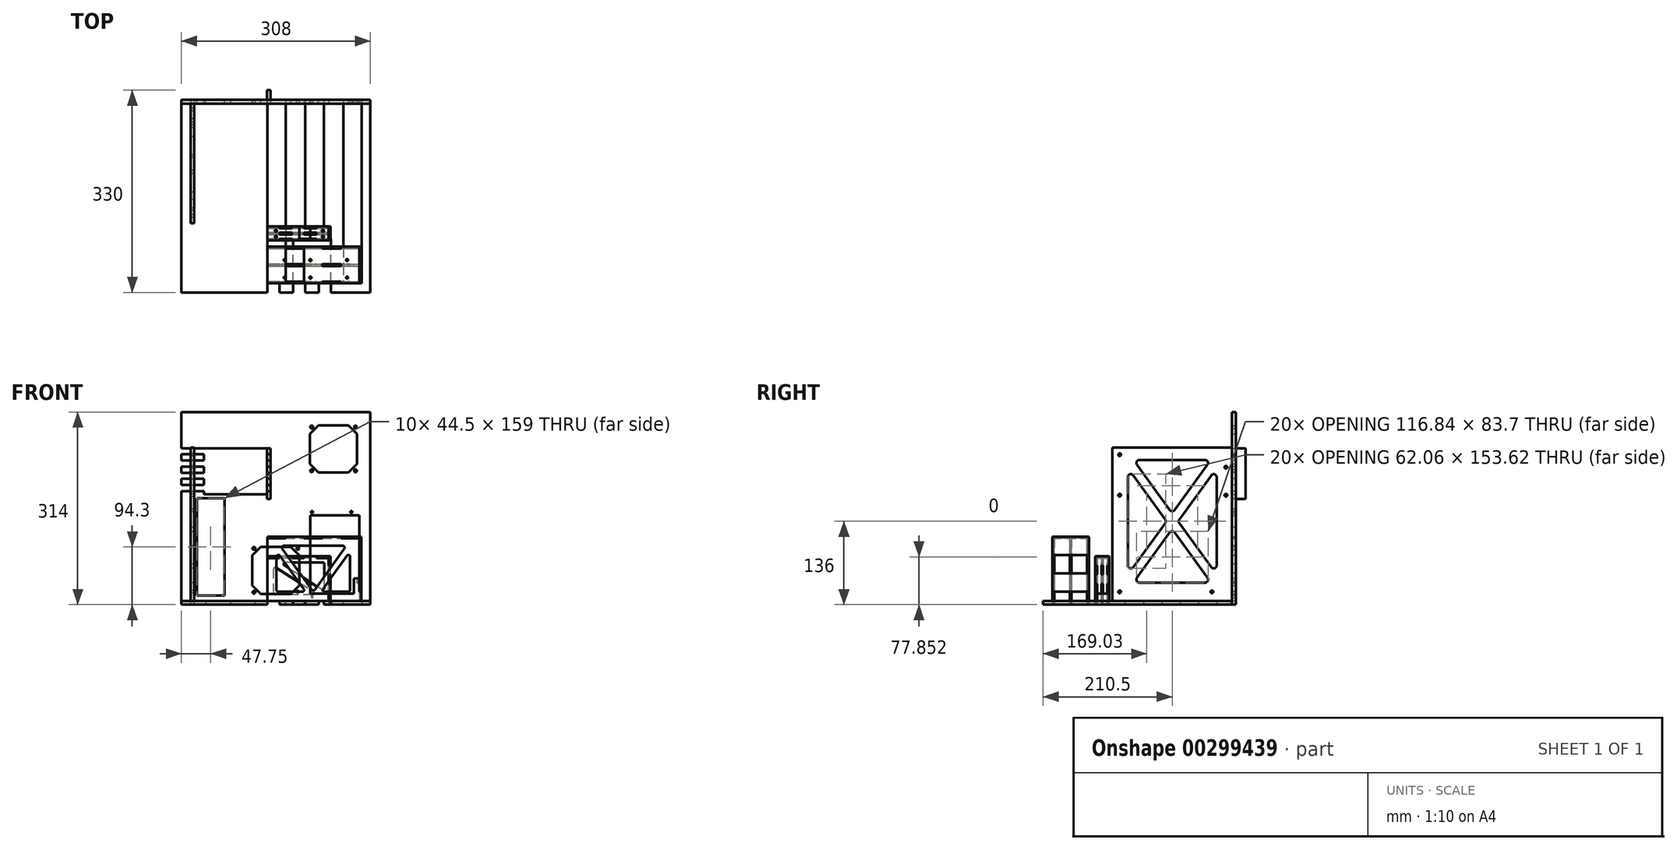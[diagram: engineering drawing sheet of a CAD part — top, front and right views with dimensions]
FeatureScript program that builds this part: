
annotation { "Feature Type Name" : "Feature", "Feature Type Description" : "" }
export const myFeature = defineFeature(function(context is Context, id is Id, definition is map)
    precondition{}
    {
        {
            var Q0;
            Q0=qCreatedBy(makeId("Top.planeOp"),FACE);
            var sketch = newSketch(context, id + "F0", { "sketchPlane" : qUnion([Q0])});
            skLineSegment(sketch, "E0.bottom", {"start": v(0, 0) * mm, "end": v(308, 0) * mm});
            skLineSegment(sketch, "E0.top", {"start": v(0, 314) * mm, "end": v(40, 314) * mm});
            skLineSegment(sketch, "E0.left", {"start": v(0, 0) * mm, "end": v(0, 314) * mm});
            skLineSegment(sketch, "E0.right", {"start": v(308, 0) * mm, "end": v(308, 308) * mm});
            skLineSegment(sketch, "E1.top", {"start": v(40, 308) * mm, "end": v(80, 308) * mm});
            skLineSegment(sketch, "E1.left", {"start": v(40, 314) * mm, "end": v(40, 308) * mm});
            skLineSegment(sketch, "E1.right", {"start": v(80, 314) * mm, "end": v(80, 308) * mm});
            skLineSegment(sketch, "E2.1.0.0", {"start": v(120, 314) * mm, "end": v(120, 308) * mm});
            skLineSegment(sketch, "E2.1.0.1", {"start": v(120, 308) * mm, "end": v(160, 308) * mm});
            skLineSegment(sketch, "E2.1.0.2", {"start": v(160, 314) * mm, "end": v(160, 308) * mm});
            skLineSegment(sketch, "E2.2.0.0", {"start": v(200, 314) * mm, "end": v(200, 308) * mm});
            skLineSegment(sketch, "E2.2.0.1", {"start": v(200, 308) * mm, "end": v(240, 308) * mm});
            skLineSegment(sketch, "E2.2.0.2", {"start": v(240, 314) * mm, "end": v(240, 308) * mm});
            skLineSegment(sketch, "E2.3.0.0", {"start": v(280, 314) * mm, "end": v(280, 308) * mm});
            skLineSegment(sketch, "E2.3.0.1", {"start": v(280, 308) * mm, "end": v(308, 308) * mm});
            skLineSegment(sketch, "E2.direction1", {"start": v(40, 308) * mm, "end": v(120, 308) * mm, "construction": true});
            skLineSegment(sketch, "E3.trimOffspring", {"start": v(160, 314) * mm, "end": v(200, 314) * mm});
            skLineSegment(sketch, "E4.trimOffspring", {"start": v(80, 314) * mm, "end": v(120, 314) * mm});
            skLineSegment(sketch, "E5.trimOffspring", {"start": v(240, 314) * mm, "end": v(280, 314) * mm});
            skSolve(sketch);
        }
        {
            var Q0;
            Q0 = qSketchRegion(id + "F0", true);
            extrude(context, id + "F1", {"entities" : qUnion([Q0]), "depth" : 6 * mm});
        }
        {
            var Q0;
            Q0=makeQuery(id+"F1.opExtrude","SWEPT_FACE",FACE,{"disambiguationData":[OSD([sQuery(id+"F0.wireOp",EDGE,"E0.top")])]});
            var sketch = newSketch(context, id + "F2", { "sketchPlane" : qUnion([Q0])});
            skLineSegment(sketch, "E6.bottom", {"start": v(0, 0) * mm, "end": v(-308, 0) * mm});
            skLineSegment(sketch, "E6.top", {"start": v(0, 314) * mm, "end": v(-308, 314) * mm});
            skLineSegment(sketch, "E6.left", {"start": v(0, 0) * mm, "end": v(0, 314) * mm});
            skLineSegment(sketch, "E6.right", {"start": v(-308, 0) * mm, "end": v(-308, 314) * mm});
            skSolve(sketch);
        }
        {
            var Q0;
            {var subQ4=sQuery(id+"F2.wireOp",EDGE,"E6.top");Q0=makeQuery(id+"F2.imprint","IMPRINT",FACE,{"disambiguationData":[TD([[makeQuery(id+"F2.imprint","IMPRINT",EDGE,{"derivedFrom":subQ4}),1.0]])]});}
            extrude(context, id + "F3", {"entities" : qUnion([Q0]), "oppositeDirection" : true, "depth" : 6 * mm});
        }
        {
            var Q0;
            Q0=makeQuery(id+"F1.opExtrude","SWEPT_BODY",BODY,{"disambiguationData":[OSD([sQuery(id+"F0.wireOp",EDGE,"E0.bottom"),sQuery(id+"F0.wireOp",EDGE,"E0.top"),sQuery(id+"F0.wireOp",EDGE,"E0.left"),sQuery(id+"F0.wireOp",EDGE,"E0.right"),sQuery(id+"F0.wireOp",EDGE,"E1.top"),sQuery(id+"F0.wireOp",EDGE,"E1.left"),sQuery(id+"F0.wireOp",EDGE,"E1.right"),sQuery(id+"F0.wireOp",EDGE,"E2.1.0.0"),sQuery(id+"F0.wireOp",EDGE,"E2.1.0.1"),sQuery(id+"F0.wireOp",EDGE,"E2.1.0.2"),sQuery(id+"F0.wireOp",EDGE,"E2.2.0.0"),sQuery(id+"F0.wireOp",EDGE,"E2.2.0.1"),sQuery(id+"F0.wireOp",EDGE,"E2.2.0.2"),sQuery(id+"F0.wireOp",EDGE,"E2.3.0.0"),sQuery(id+"F0.wireOp",EDGE,"E2.3.0.1"),sQuery(id+"F0.wireOp",EDGE,"E3.trimOffspring"),sQuery(id+"F0.wireOp",EDGE,"E4.trimOffspring"),sQuery(id+"F0.wireOp",EDGE,"E5.trimOffspring")])]});
            var Q1;
            Q1=makeQuery(id+"F3.opExtrude","SWEPT_BODY",BODY,{"disambiguationData":[OSD([sQuery(id+"F0.wireOp",EDGE,"E0.top"),sQuery(id+"F0.wireOp",EDGE,"E1.left"),sQuery(id+"F2.wireOp",EDGE,"E6.bottom"),sQuery(id+"F2.wireOp",EDGE,"E6.top"),sQuery(id+"F2.wireOp",EDGE,"E6.left"),sQuery(id+"F2.wireOp",EDGE,"E6.right")])]});
            booleanBodies(context, id + "F4", {"operationType" : BooleanOperationType.SUBTRACTION, "tools" : qUnion([Q0]), "targets" : qUnion([Q1]), "keepTools" : true});
        }
        {
            var Q0;
            Q0=makeQuery(id+"F1.opExtrude","SWEPT_FACE",FACE,{"disambiguationData":[OSD([sQuery(id+"F0.wireOp",EDGE,"E0.left")])]});
            cPlane(context, id + "F5", {"entities" : qUnion([Q0]), "cplaneType" : CPlaneType.OFFSET, "offset" : 15 * mm, "oppositeDirection" : true, "width" : 150 * mm, "height" : 150 * mm});
        }
        {
            var Q0;
            Q0=qCreatedBy(id+"F5.planeOp",FACE);
            var sketch = newSketch(context, id + "F6", { "sketchPlane" : qUnion([Q0])});
            skLineSegment(sketch, "E7.bottom", {"start": v(-284, 0) * mm, "end": v(-254, 0) * mm});
            skLineSegment(sketch, "E7.top", {"start": v(-308, 256) * mm, "end": v(-113, 256) * mm});
            skLineSegment(sketch, "E7.left", {"start": v(-314, 36) * mm, "end": v(-314, 66) * mm});
            skLineSegment(sketch, "E7.right", {"start": v(-113, 6) * mm, "end": v(-113, 256) * mm});
            skPoint(sketch, "E8", {"position": v(-298, 224.2) * mm});
            skPoint(sketch, "E9", {"position": v(-124.85, 244.52) * mm});
            skPoint(sketch, "E10", {"position": v(-124.85, 178.48) * mm});
            skPoint(sketch, "E11", {"position": v(-298, 178.48) * mm});
            skPoint(sketch, "E12", {"position": v(-275.14, 21) * mm});
            skPoint(sketch, "E13", {"position": v(-124.85, 21) * mm});
            skLineSegment(sketch, "E14.top", {"start": v(-308, 6) * mm, "end": v(-284, 6) * mm});
            skLineSegment(sketch, "E14.right", {"start": v(-284, 0) * mm, "end": v(-284, 6) * mm});
            skLineSegment(sketch, "E15.1.0.0", {"start": v(-224, 0) * mm, "end": v(-224, 6) * mm});
            skLineSegment(sketch, "E15.1.0.1", {"start": v(-254, 6) * mm, "end": v(-224, 6) * mm});
            skLineSegment(sketch, "E15.1.0.2", {"start": v(-254, 0) * mm, "end": v(-254, 6) * mm});
            skLineSegment(sketch, "E15.2.0.0", {"start": v(-164, 0) * mm, "end": v(-164, 6) * mm});
            skLineSegment(sketch, "E15.2.0.1", {"start": v(-194, 6) * mm, "end": v(-164, 6) * mm});
            skLineSegment(sketch, "E15.2.0.2", {"start": v(-194, 0) * mm, "end": v(-194, 6) * mm});
            skLineSegment(sketch, "E15.3.0.1", {"start": v(-134, 6) * mm, "end": v(-113, 6) * mm});
            skLineSegment(sketch, "E15.3.0.2", {"start": v(-134, 0) * mm, "end": v(-134, 6) * mm});
            skLineSegment(sketch, "E15.direction1", {"start": v(-284, 0) * mm, "end": v(-254, 0) * mm, "construction": true});
            skLineSegment(sketch, "E16.trimOffspring", {"start": v(-164, 0) * mm, "end": v(-134, 0) * mm});
            skLineSegment(sketch, "E17.trimOffspring", {"start": v(-224, 0) * mm, "end": v(-194, 0) * mm});
            skLineSegment(sketch, "E18.top", {"start": v(-314, 36) * mm, "end": v(-308, 36) * mm});
            skLineSegment(sketch, "E18.right", {"start": v(-308, 6) * mm, "end": v(-308, 36) * mm});
            skLineSegment(sketch, "E19.0.1.0", {"start": v(-308, 66) * mm, "end": v(-308, 96) * mm});
            skLineSegment(sketch, "E19.0.1.1", {"start": v(-314, 96) * mm, "end": v(-308, 96) * mm});
            skLineSegment(sketch, "E19.0.1.2", {"start": v(-314, 66) * mm, "end": v(-308, 66) * mm});
            skLineSegment(sketch, "E19.0.2.0", {"start": v(-308, 126) * mm, "end": v(-308, 156) * mm});
            skLineSegment(sketch, "E19.0.2.1", {"start": v(-314, 156) * mm, "end": v(-308, 156) * mm});
            skLineSegment(sketch, "E19.0.2.2", {"start": v(-314, 126) * mm, "end": v(-308, 126) * mm});
            skLineSegment(sketch, "E19.0.3.0", {"start": v(-308, 186) * mm, "end": v(-308, 216) * mm});
            skLineSegment(sketch, "E19.0.3.1", {"start": v(-314, 216) * mm, "end": v(-308, 216) * mm});
            skLineSegment(sketch, "E19.0.3.2", {"start": v(-314, 186) * mm, "end": v(-308, 186) * mm});
            skLineSegment(sketch, "E19.0.4.0", {"start": v(-308, 246) * mm, "end": v(-308, 256) * mm});
            skLineSegment(sketch, "E19.0.4.2", {"start": v(-314, 246) * mm, "end": v(-308, 246) * mm});
            skLineSegment(sketch, "E19.direction1", {"start": v(-325.44, 6) * mm, "end": v(-314, 6) * mm, "construction": true});
            skLineSegment(sketch, "E19.direction2", {"start": v(-314, 36) * mm, "end": v(-314, 66) * mm, "construction": true});
            skLineSegment(sketch, "E20.trimOffspring", {"start": v(-314, 96) * mm, "end": v(-314, 126) * mm});
            skLineSegment(sketch, "E21.trimOffspring", {"start": v(-314, 156) * mm, "end": v(-314, 186) * mm});
            skLineSegment(sketch, "E22.trimOffspring", {"start": v(-314, 216) * mm, "end": v(-314, 246) * mm});
            skLineSegment(sketch, "E23.bottom", {"start": v(-283, 236) * mm, "end": v(-138, 236) * mm, "construction": true});
            skLineSegment(sketch, "E23.top", {"start": v(-283, 36) * mm, "end": v(-138, 36) * mm, "construction": true});
            skLineSegment(sketch, "E23.left", {"start": v(-283, 236) * mm, "end": v(-283, 36) * mm, "construction": true});
            skLineSegment(sketch, "E23.right", {"start": v(-138, 236) * mm, "end": v(-138, 36) * mm, "construction": true});
            skLineSegment(sketch, "E24", {"start": v(-283, 236) * mm, "end": v(-138, 36) * mm, "construction": true});
            skLineSegment(sketch, "E25", {"start": v(-283, 36) * mm, "end": v(-138, 236) * mm, "construction": true});
            skLineSegment(sketch, "E26", {"start": v(-138, 223.22) * mm, "end": v(-201.24, 136) * mm});
            skLineSegment(sketch, "E27", {"start": v(-201.24, 136) * mm, "end": v(-138, 48.78) * mm});
            skLineSegment(sketch, "E28", {"start": v(-147.26, 236) * mm, "end": v(-210.5, 148.78) * mm});
            skLineSegment(sketch, "E29", {"start": v(-210.5, 148.78) * mm, "end": v(-273.74, 236) * mm});
            skLineSegment(sketch, "E30", {"start": v(-147.26, 36) * mm, "end": v(-210.5, 123.22) * mm});
            skLineSegment(sketch, "E31", {"start": v(-210.5, 123.22) * mm, "end": v(-273.74, 36) * mm});
            skLineSegment(sketch, "E32", {"start": v(-283, 223.22) * mm, "end": v(-219.76, 136) * mm});
            skLineSegment(sketch, "E33", {"start": v(-219.76, 136) * mm, "end": v(-283, 48.78) * mm});
            skLineSegment(sketch, "E34", {"start": v(-273.74, 36) * mm, "end": v(-147.26, 36) * mm});
            skLineSegment(sketch, "E35", {"start": v(-138, 223.22) * mm, "end": v(-138, 48.78) * mm});
            skLineSegment(sketch, "E36", {"start": v(-273.74, 236) * mm, "end": v(-147.26, 236) * mm});
            skLineSegment(sketch, "E37", {"start": v(-283, 223.22) * mm, "end": v(-283, 48.78) * mm});
            skSolve(sketch);
        }
        {
            var Q0;
            Q0=makeQuery(id+"F6.imprint","IMPRINT",FACE,{"disambiguationData":[TD([[makeQuery(id+"F6.imprint","IMPRINT",EDGE,{"derivedFrom":sQuery(id+"F6.wireOp",EDGE,"E7.bottom")}),1.0]])]});
            extrude(context, id + "F7", {"entities" : qUnion([Q0]), "oppositeDirection" : true, "depth" : 6 * mm});
        }
        {
            var Q0;
            Q0=makeQuery(id+"F7.opExtrude","SWEPT_BODY",BODY,{"disambiguationData":[OSD([sQuery(id+"F6.wireOp",EDGE,"E7.bottom"),sQuery(id+"F6.wireOp",EDGE,"E7.top"),sQuery(id+"F6.wireOp",EDGE,"E7.left"),sQuery(id+"F6.wireOp",EDGE,"E7.right"),sQuery(id+"F6.wireOp",EDGE,"E14.top"),sQuery(id+"F6.wireOp",EDGE,"E14.right"),sQuery(id+"F6.wireOp",EDGE,"E15.1.0.0"),sQuery(id+"F6.wireOp",EDGE,"E15.1.0.1"),sQuery(id+"F6.wireOp",EDGE,"E15.1.0.2"),sQuery(id+"F6.wireOp",EDGE,"E15.2.0.0"),sQuery(id+"F6.wireOp",EDGE,"E15.2.0.1"),sQuery(id+"F6.wireOp",EDGE,"E15.2.0.2"),sQuery(id+"F6.wireOp",EDGE,"E15.3.0.1"),sQuery(id+"F6.wireOp",EDGE,"E15.3.0.2"),sQuery(id+"F6.wireOp",EDGE,"E16.trimOffspring"),sQuery(id+"F6.wireOp",EDGE,"E17.trimOffspring"),sQuery(id+"F6.wireOp",EDGE,"E18.top"),sQuery(id+"F6.wireOp",EDGE,"E18.right"),sQuery(id+"F6.wireOp",EDGE,"E19.0.1.0"),sQuery(id+"F6.wireOp",EDGE,"E19.0.1.1"),sQuery(id+"F6.wireOp",EDGE,"E19.0.1.2"),sQuery(id+"F6.wireOp",EDGE,"E19.0.2.0"),sQuery(id+"F6.wireOp",EDGE,"E19.0.2.1"),sQuery(id+"F6.wireOp",EDGE,"E19.0.2.2"),sQuery(id+"F6.wireOp",EDGE,"E19.0.3.0"),sQuery(id+"F6.wireOp",EDGE,"E19.0.3.1"),sQuery(id+"F6.wireOp",EDGE,"E19.0.3.2"),sQuery(id+"F6.wireOp",EDGE,"E19.0.4.0"),sQuery(id+"F6.wireOp",EDGE,"E19.0.4.2"),sQuery(id+"F6.wireOp",EDGE,"E20.trimOffspring"),sQuery(id+"F6.wireOp",EDGE,"E21.trimOffspring"),sQuery(id+"F6.wireOp",EDGE,"E22.trimOffspring")])]});
            var Q1;
            Q1=makeQuery(id+"F3.opExtrude","SWEPT_BODY",BODY,{"disambiguationData":[OSD([sQuery(id+"F0.wireOp",EDGE,"E0.top"),sQuery(id+"F0.wireOp",EDGE,"E1.left"),sQuery(id+"F2.wireOp",EDGE,"E6.bottom"),sQuery(id+"F2.wireOp",EDGE,"E6.top"),sQuery(id+"F2.wireOp",EDGE,"E6.left"),sQuery(id+"F2.wireOp",EDGE,"E6.right")])]});
            booleanBodies(context, id + "F8", {"operationType" : BooleanOperationType.SUBTRACTION, "tools" : qUnion([Q0]), "targets" : qUnion([Q1]), "keepTools" : true});
        }
        {
            var Q0;
            Q0=makeQuery(id+"F7.opExtrude","SWEPT_BODY",BODY,{"disambiguationData":[OSD([sQuery(id+"F6.wireOp",EDGE,"E7.bottom"),sQuery(id+"F6.wireOp",EDGE,"E7.top"),sQuery(id+"F6.wireOp",EDGE,"E7.left"),sQuery(id+"F6.wireOp",EDGE,"E7.right"),sQuery(id+"F6.wireOp",EDGE,"E14.top"),sQuery(id+"F6.wireOp",EDGE,"E14.right"),sQuery(id+"F6.wireOp",EDGE,"E15.1.0.0"),sQuery(id+"F6.wireOp",EDGE,"E15.1.0.1"),sQuery(id+"F6.wireOp",EDGE,"E15.1.0.2"),sQuery(id+"F6.wireOp",EDGE,"E15.2.0.0"),sQuery(id+"F6.wireOp",EDGE,"E15.2.0.1"),sQuery(id+"F6.wireOp",EDGE,"E15.2.0.2"),sQuery(id+"F6.wireOp",EDGE,"E15.3.0.1"),sQuery(id+"F6.wireOp",EDGE,"E15.3.0.2"),sQuery(id+"F6.wireOp",EDGE,"E16.trimOffspring"),sQuery(id+"F6.wireOp",EDGE,"E17.trimOffspring"),sQuery(id+"F6.wireOp",EDGE,"E18.top"),sQuery(id+"F6.wireOp",EDGE,"E18.right"),sQuery(id+"F6.wireOp",EDGE,"E19.0.1.0"),sQuery(id+"F6.wireOp",EDGE,"E19.0.1.1"),sQuery(id+"F6.wireOp",EDGE,"E19.0.1.2"),sQuery(id+"F6.wireOp",EDGE,"E19.0.2.0"),sQuery(id+"F6.wireOp",EDGE,"E19.0.2.1"),sQuery(id+"F6.wireOp",EDGE,"E19.0.2.2"),sQuery(id+"F6.wireOp",EDGE,"E19.0.3.0"),sQuery(id+"F6.wireOp",EDGE,"E19.0.3.1"),sQuery(id+"F6.wireOp",EDGE,"E19.0.3.2"),sQuery(id+"F6.wireOp",EDGE,"E19.0.4.0"),sQuery(id+"F6.wireOp",EDGE,"E19.0.4.2"),sQuery(id+"F6.wireOp",EDGE,"E20.trimOffspring"),sQuery(id+"F6.wireOp",EDGE,"E21.trimOffspring"),sQuery(id+"F6.wireOp",EDGE,"E22.trimOffspring")])]});
            var Q1;
            Q1=makeQuery(id+"F1.opExtrude","SWEPT_BODY",BODY,{"disambiguationData":[OSD([sQuery(id+"F0.wireOp",EDGE,"E0.bottom"),sQuery(id+"F0.wireOp",EDGE,"E0.top"),sQuery(id+"F0.wireOp",EDGE,"E0.left"),sQuery(id+"F0.wireOp",EDGE,"E0.right"),sQuery(id+"F0.wireOp",EDGE,"E1.top"),sQuery(id+"F0.wireOp",EDGE,"E1.left"),sQuery(id+"F0.wireOp",EDGE,"E1.right"),sQuery(id+"F0.wireOp",EDGE,"E2.1.0.0"),sQuery(id+"F0.wireOp",EDGE,"E2.1.0.1"),sQuery(id+"F0.wireOp",EDGE,"E2.1.0.2"),sQuery(id+"F0.wireOp",EDGE,"E2.2.0.0"),sQuery(id+"F0.wireOp",EDGE,"E2.2.0.1"),sQuery(id+"F0.wireOp",EDGE,"E2.2.0.2"),sQuery(id+"F0.wireOp",EDGE,"E2.3.0.0"),sQuery(id+"F0.wireOp",EDGE,"E2.3.0.1"),sQuery(id+"F0.wireOp",EDGE,"E3.trimOffspring"),sQuery(id+"F0.wireOp",EDGE,"E4.trimOffspring"),sQuery(id+"F0.wireOp",EDGE,"E5.trimOffspring")])]});
            booleanBodies(context, id + "F9", {"operationType" : BooleanOperationType.SUBTRACTION, "tools" : qUnion([Q0]), "targets" : qUnion([Q1]), "keepTools" : true});
        }
        {
            var Q0;
            Q0=sQuery(id+"F6.wireOp",VERTEX,"E8");
            var Q1;
            Q1=sQuery(id+"F6.wireOp",VERTEX,"E11");
            var Q2;
            Q2=sQuery(id+"F6.wireOp",VERTEX,"E12");
            var Q3;
            Q3=sQuery(id+"F6.wireOp",VERTEX,"E13");
            var Q4;
            Q4=sQuery(id+"F6.wireOp",VERTEX,"E10");
            var Q5;
            Q5=sQuery(id+"F6.wireOp",VERTEX,"E9");
            var Q6;
            Q6=makeQuery(id+"F7.opExtrude","SWEPT_BODY",BODY,{"disambiguationData":[OSD([sQuery(id+"F6.wireOp",EDGE,"E7.bottom"),sQuery(id+"F6.wireOp",EDGE,"E7.top"),sQuery(id+"F6.wireOp",EDGE,"E7.left"),sQuery(id+"F6.wireOp",EDGE,"E7.right"),sQuery(id+"F6.wireOp",EDGE,"E14.top"),sQuery(id+"F6.wireOp",EDGE,"E14.right"),sQuery(id+"F6.wireOp",EDGE,"E15.1.0.0"),sQuery(id+"F6.wireOp",EDGE,"E15.1.0.1"),sQuery(id+"F6.wireOp",EDGE,"E15.1.0.2"),sQuery(id+"F6.wireOp",EDGE,"E15.2.0.0"),sQuery(id+"F6.wireOp",EDGE,"E15.2.0.1"),sQuery(id+"F6.wireOp",EDGE,"E15.2.0.2"),sQuery(id+"F6.wireOp",EDGE,"E15.3.0.1"),sQuery(id+"F6.wireOp",EDGE,"E15.3.0.2"),sQuery(id+"F6.wireOp",EDGE,"E16.trimOffspring"),sQuery(id+"F6.wireOp",EDGE,"E17.trimOffspring"),sQuery(id+"F6.wireOp",EDGE,"E18.top"),sQuery(id+"F6.wireOp",EDGE,"E18.right"),sQuery(id+"F6.wireOp",EDGE,"E19.0.1.0"),sQuery(id+"F6.wireOp",EDGE,"E19.0.1.1"),sQuery(id+"F6.wireOp",EDGE,"E19.0.1.2"),sQuery(id+"F6.wireOp",EDGE,"E19.0.2.0"),sQuery(id+"F6.wireOp",EDGE,"E19.0.2.1"),sQuery(id+"F6.wireOp",EDGE,"E19.0.2.2"),sQuery(id+"F6.wireOp",EDGE,"E19.0.3.0"),sQuery(id+"F6.wireOp",EDGE,"E19.0.3.1"),sQuery(id+"F6.wireOp",EDGE,"E19.0.3.2"),sQuery(id+"F6.wireOp",EDGE,"E19.0.4.0"),sQuery(id+"F6.wireOp",EDGE,"E19.0.4.2"),sQuery(id+"F6.wireOp",EDGE,"E20.trimOffspring"),sQuery(id+"F6.wireOp",EDGE,"E21.trimOffspring"),sQuery(id+"F6.wireOp",EDGE,"E22.trimOffspring")])]});
            hole(context, id + "F10", {"style" : HoleStyle.SIMPLE, "endStyle" : HoleEndStyle.THROUGH, "standardTappedOrClearance" : lookupTablePath({ "standard" : "ISO", "fit" : "Normal", "size" : "M4", "type" : "Clearance" }), "standardBlindInLast" : lookupTablePath({ "fit" : "Standard", "standard" : "ISO", "size" : "M4", "type" : "Clearance" }), "holeDiameter" : 4.4 * mm, "tappedDepth" : 6 * mm, "tapClearance" : 3, "locations" : qUnion([Q0, Q1, Q2, Q3, Q4, Q5]), "scope" : qUnion([Q6])});
        }
        {
            var Q0;
            Q0=makeQuery(id+"F7.opExtrude","SWEPT_EDGE",EDGE,{"disambiguationData":[OSD([sQuery(id+"F6.wireOp",EDGE,"E32"),sQuery(id+"F6.wireOp",EDGE,"E37")])]});
            var Q1;
            Q1=makeQuery(id+"F7.opExtrude","SWEPT_EDGE",EDGE,{"disambiguationData":[OSD([sQuery(id+"F6.wireOp",EDGE,"E30"),sQuery(id+"F6.wireOp",EDGE,"E31")])]});
            var Q2;
            Q2=makeQuery(id+"F7.opExtrude","SWEPT_EDGE",EDGE,{"disambiguationData":[OSD([sQuery(id+"F6.wireOp",EDGE,"E30"),sQuery(id+"F6.wireOp",EDGE,"E34")])]});
            var Q3;
            Q3=makeQuery(id+"F7.opExtrude","SWEPT_EDGE",EDGE,{"disambiguationData":[OSD([sQuery(id+"F6.wireOp",EDGE,"E27"),sQuery(id+"F6.wireOp",EDGE,"E35")])]});
            var Q4;
            Q4=makeQuery(id+"F7.opExtrude","SWEPT_EDGE",EDGE,{"disambiguationData":[OSD([sQuery(id+"F6.wireOp",EDGE,"E26"),sQuery(id+"F6.wireOp",EDGE,"E27")])]});
            var Q5;
            Q5=makeQuery(id+"F7.opExtrude","SWEPT_EDGE",EDGE,{"disambiguationData":[OSD([sQuery(id+"F6.wireOp",EDGE,"E26"),sQuery(id+"F6.wireOp",EDGE,"E35")])]});
            var Q6;
            Q6=makeQuery(id+"F7.opExtrude","SWEPT_EDGE",EDGE,{"disambiguationData":[OSD([sQuery(id+"F6.wireOp",EDGE,"E28"),sQuery(id+"F6.wireOp",EDGE,"E36")])]});
            var Q7;
            Q7=makeQuery(id+"F7.opExtrude","SWEPT_EDGE",EDGE,{"disambiguationData":[OSD([sQuery(id+"F6.wireOp",EDGE,"E28"),sQuery(id+"F6.wireOp",EDGE,"E29")])]});
            var Q8;
            Q8=makeQuery(id+"F7.opExtrude","SWEPT_EDGE",EDGE,{"disambiguationData":[OSD([sQuery(id+"F6.wireOp",EDGE,"E32"),sQuery(id+"F6.wireOp",EDGE,"E33")])]});
            var Q9;
            Q9=makeQuery(id+"F7.opExtrude","SWEPT_EDGE",EDGE,{"disambiguationData":[OSD([sQuery(id+"F6.wireOp",EDGE,"E33"),sQuery(id+"F6.wireOp",EDGE,"E37")])]});
            var Q10;
            Q10=makeQuery(id+"F7.opExtrude","SWEPT_EDGE",EDGE,{"disambiguationData":[OSD([sQuery(id+"F6.wireOp",EDGE,"E31"),sQuery(id+"F6.wireOp",EDGE,"E34")])]});
            var Q11;
            Q11=makeQuery(id+"F7.opExtrude","SWEPT_EDGE",EDGE,{"disambiguationData":[OSD([sQuery(id+"F6.wireOp",EDGE,"E29"),sQuery(id+"F6.wireOp",EDGE,"E36")])]});
            fillet(context, id + "F11", {"entities" : qUnion([Q0, Q1, Q2, Q3, Q4, Q5, Q6, Q7, Q8, Q9, Q10, Q11]), "radius" : 5 * mm, "tangentPropagation" : true, "allowEdgeOverflow" : false});
        }
        {
            var Q0;
            Q0=makeQuery(id+"F3.opExtrude","CAP_FACE",FACE,{"disambiguationData":[OSD([sQuery(id+"F0.wireOp",EDGE,"E0.top"),sQuery(id+"F0.wireOp",EDGE,"E1.left"),sQuery(id+"F2.wireOp",EDGE,"E6.bottom"),sQuery(id+"F2.wireOp",EDGE,"E6.top"),sQuery(id+"F2.wireOp",EDGE,"E6.left"),sQuery(id+"F2.wireOp",EDGE,"E6.right")])],"isStart":true});
            var sketch = newSketch(context, id + "F12", { "sketchPlane" : qUnion([Q0])});
            skLineSegment(sketch, "E38", {"start": v(-27.8, 249.88) * mm, "end": v(-27.8, 20.43) * mm, "construction": true});
            skLineSegment(sketch, "E39.bottom", {"start": v(-70, 14.8) * mm, "end": v(-25.5, 14.8) * mm});
            skLineSegment(sketch, "E39.top", {"start": v(-70, 173.8) * mm, "end": v(-25.5, 173.8) * mm});
            skLineSegment(sketch, "E39.left", {"start": v(-70, 14.8) * mm, "end": v(-70, 173.8) * mm});
            skLineSegment(sketch, "E39.right", {"start": v(-25.5, 14.8) * mm, "end": v(-25.5, 173.8) * mm});
            skLineSegment(sketch, "E40.bottom", {"start": v(-139.3, 180.15) * mm, "end": v(-36.6, 180.15) * mm});
            skLineSegment(sketch, "E40.top", {"start": v(-139.3, 255.08) * mm, "end": v(-36.6, 255.08) * mm});
            skLineSegment(sketch, "E40.left", {"start": v(-139.3, 180.15) * mm, "end": v(-139.3, 255.08) * mm});
            skLineSegment(sketch, "E40.right", {"start": v(-36.6, 180.15) * mm, "end": v(-36.6, 255.08) * mm});
            skLineSegment(sketch, "E41", {"start": v(-139.3, 172.88) * mm, "end": v(-139.3, 270.63) * mm, "construction": true});
            skSolve(sketch);
        }
        {
            var Q0;
            Q0 = qSketchRegion(id + "F12", true);
            extrude(context, id + "F13", {"entities" : qUnion([Q0]), "operationType" : NewBodyOperationType.REMOVE, "endBound" : BoundingType.THROUGH_ALL, "oppositeDirection" : true, "depth" : 25 * mm});
        }
        {
            var Q0;
            Q0=sQuery(id+"F12.wireOp",EDGE,"E41");
            var Q1;
            Q1=qCreatedBy(makeId("Right.planeOp"),FACE);
            cPlane(context, id + "F14", {"entities" : qUnion([Q0, Q1]), "cplaneType" : CPlaneType.LINE_ANGLE, "offset" : 25 * mm, "angle" : 0 * degree, "width" : 150 * mm, "height" : 150 * mm});
        }
        {
            var Q0;
            Q0=qCreatedBy(id+"F14.planeOp",FACE);
            var sketch = newSketch(context, id + "F15", { "sketchPlane" : qUnion([Q0])});
            skLineSegment(sketch, "E42", {"start": v(-345.36, 180.15) * mm, "end": v(-318, 180.15) * mm, "construction": true});
            skLineSegment(sketch, "E43.bottom", {"start": v(-330, 255.08) * mm, "end": v(-308, 255.08) * mm});
            skLineSegment(sketch, "E43.top", {"start": v(-330, 172.15) * mm, "end": v(-308, 172.15) * mm});
            skLineSegment(sketch, "E43.left", {"start": v(-330, 255.08) * mm, "end": v(-330, 172.15) * mm});
            skLineSegment(sketch, "E43.right", {"start": v(-308, 255.08) * mm, "end": v(-308, 172.15) * mm});
            skSolve(sketch);
        }
        {
            var Q0;
            Q0 = qSketchRegion(id + "F15", true);
            extrude(context, id + "F16", {"entities" : qUnion([Q0]), "oppositeDirection" : true, "depth" : 6 * mm});
        }
        {
            var Q0;
            Q0=makeQuery(id+"F16.opExtrude","CAP_FACE",FACE,{"disambiguationData":[OSD([sQuery(id+"F15.wireOp",EDGE,"E43.bottom"),sQuery(id+"F15.wireOp",EDGE,"E43.top"),sQuery(id+"F15.wireOp",EDGE,"E43.left"),sQuery(id+"F15.wireOp",EDGE,"E43.right")])],"isStart":false});
            var sketch = newSketch(context, id + "F17", { "sketchPlane" : qUnion([Q0])});
            skLineSegment(sketch, "E44.bottom", {"start": v(308, 255.08) * mm, "end": v(314, 255.08) * mm});
            skLineSegment(sketch, "E44.top", {"start": v(308, 245.08) * mm, "end": v(314, 245.08) * mm});
            skLineSegment(sketch, "E44.left", {"start": v(308, 255.08) * mm, "end": v(308, 245.08) * mm});
            skLineSegment(sketch, "E44.right", {"start": v(314, 255.08) * mm, "end": v(314, 245.08) * mm});
            skLineSegment(sketch, "E45.0.1.0", {"start": v(308, 225.08) * mm, "end": v(314, 225.08) * mm});
            skLineSegment(sketch, "E45.0.1.1", {"start": v(314, 235.08) * mm, "end": v(314, 225.08) * mm});
            skLineSegment(sketch, "E45.0.1.2", {"start": v(308, 235.08) * mm, "end": v(314, 235.08) * mm});
            skLineSegment(sketch, "E45.0.1.3", {"start": v(308, 235.08) * mm, "end": v(308, 225.08) * mm});
            skLineSegment(sketch, "E45.0.2.0", {"start": v(308, 205.08) * mm, "end": v(314, 205.08) * mm});
            skLineSegment(sketch, "E45.0.2.1", {"start": v(314, 215.08) * mm, "end": v(314, 205.08) * mm});
            skLineSegment(sketch, "E45.0.2.2", {"start": v(308, 215.08) * mm, "end": v(314, 215.08) * mm});
            skLineSegment(sketch, "E45.0.2.3", {"start": v(308, 215.08) * mm, "end": v(308, 205.08) * mm});
            skLineSegment(sketch, "E45.0.3.0", {"start": v(308, 185.08) * mm, "end": v(314, 185.08) * mm});
            skLineSegment(sketch, "E45.0.3.1", {"start": v(314, 195.08) * mm, "end": v(314, 185.08) * mm});
            skLineSegment(sketch, "E45.0.3.2", {"start": v(308, 195.08) * mm, "end": v(314, 195.08) * mm});
            skLineSegment(sketch, "E45.0.3.3", {"start": v(308, 195.08) * mm, "end": v(308, 185.08) * mm});
            skLineSegment(sketch, "E45.direction1", {"start": v(308, 245.08) * mm, "end": v(333, 245.08) * mm, "construction": true});
            skLineSegment(sketch, "E45.direction2", {"start": v(308, 245.08) * mm, "end": v(308, 225.08) * mm, "construction": true});
            skSolve(sketch);
        }
        {
            var Q0;
            Q0 = qSketchRegion(id + "F17", true);
            extrude(context, id + "F18", {"entities" : qUnion([Q0]), "operationType" : NewBodyOperationType.REMOVE, "endBound" : BoundingType.THROUGH_ALL, "oppositeDirection" : true, "depth" : 25 * mm});
        }
        {
            var Q0;
            Q0=makeQuery(id+"F16.opExtrude","SWEPT_BODY",BODY,{"disambiguationData":[OSD([sQuery(id+"F15.wireOp",EDGE,"E43.bottom"),sQuery(id+"F15.wireOp",EDGE,"E43.top"),sQuery(id+"F15.wireOp",EDGE,"E43.left"),sQuery(id+"F15.wireOp",EDGE,"E43.right")])]});
            var Q1;
            Q1=makeQuery(id+"F3.opExtrude","SWEPT_BODY",BODY,{"disambiguationData":[OSD([sQuery(id+"F0.wireOp",EDGE,"E0.top"),sQuery(id+"F0.wireOp",EDGE,"E1.left"),sQuery(id+"F2.wireOp",EDGE,"E6.bottom"),sQuery(id+"F2.wireOp",EDGE,"E6.top"),sQuery(id+"F2.wireOp",EDGE,"E6.left"),sQuery(id+"F2.wireOp",EDGE,"E6.right")])]});
            booleanBodies(context, id + "F19", {"operationType" : BooleanOperationType.SUBTRACTION, "tools" : qUnion([Q0]), "targets" : qUnion([Q1]), "keepTools" : true});
        }
        {
            var Q0;
            Q0=makeQuery(id+"F3.opExtrude","CAP_FACE",FACE,{"disambiguationData":[OSD([sQuery(id+"F0.wireOp",EDGE,"E0.top"),sQuery(id+"F0.wireOp",EDGE,"E1.left"),sQuery(id+"F2.wireOp",EDGE,"E6.bottom"),sQuery(id+"F2.wireOp",EDGE,"E6.top"),sQuery(id+"F2.wireOp",EDGE,"E6.left"),sQuery(id+"F2.wireOp",EDGE,"E6.right")])],"isStart":true});
            var sketch = newSketch(context, id + "F20", { "sketchPlane" : qUnion([Q0])});
            skPoint(sketch, "E46", {"position": v(-213, 13) * mm});
            skPoint(sketch, "E47", {"position": v(-287, 37) * mm});
            skPoint(sketch, "E48", {"position": v(-277, 151) * mm});
            skPoint(sketch, "E49", {"position": v(-213, 151) * mm});
            skLineSegment(sketch, "E50", {"start": v(-293, 0) * mm, "end": v(-293, 156) * mm, "construction": true});
            skLineSegment(sketch, "E51", {"start": v(-207, 0) * mm, "end": v(-207, 156) * mm, "construction": true});
            skLineSegment(sketch, "E52", {"start": v(-293, 156) * mm, "end": v(-207, 156) * mm, "construction": true});
            skLineSegment(sketch, "E53.bottom", {"start": v(-290, 146) * mm, "end": v(-210, 146) * mm});
            skLineSegment(sketch, "E53.top", {"start": v(-281, 18) * mm, "end": v(-210, 18) * mm});
            skLineSegment(sketch, "E53.right", {"start": v(-210, 146) * mm, "end": v(-210, 18) * mm});
            skLineSegment(sketch, "E54", {"start": v(-290, 146) * mm, "end": v(-290, 43) * mm});
            skLineSegment(sketch, "E55", {"start": v(-290, 43) * mm, "end": v(-281, 43) * mm});
            skLineSegment(sketch, "E56", {"start": v(-281, 18) * mm, "end": v(-281, 43) * mm});
            skSolve(sketch);
        }
        {
            var Q0;
            Q0=makeQuery(id+"F20.imprint","IMPRINT",FACE,{"disambiguationData":[TD([[makeQuery(id+"F20.imprint","IMPRINT",EDGE,{"derivedFrom":sQuery(id+"F20.wireOp",EDGE,"E53.bottom")}),-1.0]])]});
            extrude(context, id + "F21", {"entities" : qUnion([Q0]), "operationType" : NewBodyOperationType.REMOVE, "endBound" : BoundingType.THROUGH_ALL, "oppositeDirection" : true, "depth" : 25 * mm});
        }
        {
            var Q0;
            Q0=sQuery(id+"F20.wireOp",VERTEX,"E48");
            var Q1;
            Q1=sQuery(id+"F20.wireOp",VERTEX,"E47");
            var Q2;
            Q2=sQuery(id+"F20.wireOp",VERTEX,"E46");
            var Q3;
            Q3=sQuery(id+"F20.wireOp",VERTEX,"E49");
            var Q4;
            Q4=makeQuery(id+"F3.opExtrude","SWEPT_BODY",BODY,{"disambiguationData":[OSD([sQuery(id+"F0.wireOp",EDGE,"E0.top"),sQuery(id+"F0.wireOp",EDGE,"E1.left"),sQuery(id+"F2.wireOp",EDGE,"E6.bottom"),sQuery(id+"F2.wireOp",EDGE,"E6.top"),sQuery(id+"F2.wireOp",EDGE,"E6.left"),sQuery(id+"F2.wireOp",EDGE,"E6.right")])]});
            hole(context, id + "F22", {"style" : HoleStyle.SIMPLE, "endStyle" : HoleEndStyle.THROUGH, "standardTappedOrClearance" : lookupTablePath({ "standard" : "ISO", "fit" : "Normal", "size" : "M3", "type" : "Clearance" }), "standardBlindInLast" : lookupTablePath({ "fit" : "Standard", "standard" : "ISO", "size" : "M3", "type" : "Clearance" }), "holeDiameter" : 3.3 * mm, "tappedDepth" : 6 * mm, "tapClearance" : 3, "locations" : qUnion([Q0, Q1, Q2, Q3]), "scope" : qUnion([Q4])});
        }
        {
            var Q0;
            Q0=makeQuery(id+"F3.opExtrude","CAP_FACE",FACE,{"disambiguationData":[OSD([sQuery(id+"F0.wireOp",EDGE,"E0.top"),sQuery(id+"F0.wireOp",EDGE,"E1.left"),sQuery(id+"F2.wireOp",EDGE,"E6.bottom"),sQuery(id+"F2.wireOp",EDGE,"E6.top"),sQuery(id+"F2.wireOp",EDGE,"E6.left"),sQuery(id+"F2.wireOp",EDGE,"E6.right")])],"isStart":true});
            var sketch = newSketch(context, id + "F23", { "sketchPlane" : qUnion([Q0])});
            skLineSegment(sketch, "E57.bottom", {"start": v(-114, 16) * mm, "end": v(-194, 16) * mm, "construction": true});
            skLineSegment(sketch, "E57.top", {"start": v(-114, 96) * mm, "end": v(-194, 96) * mm, "construction": true});
            skLineSegment(sketch, "E57.left", {"start": v(-114, 16) * mm, "end": v(-114, 96) * mm, "construction": true});
            skLineSegment(sketch, "E57.right", {"start": v(-194, 16) * mm, "end": v(-194, 96) * mm, "construction": true});
            skPoint(sketch, "E57.middle", {"position": v(-154, 56) * mm});
            skPoint(sketch, "E58", {"position": v(-189.75, 91.75) * mm});
            skPoint(sketch, "E59", {"position": v(-118.25, 91.75) * mm});
            skPoint(sketch, "E60", {"position": v(-118.25, 20.25) * mm});
            skPoint(sketch, "E61", {"position": v(-189.75, 20.25) * mm});
            skLineSegment(sketch, "E62", {"start": v(-154, 314) * mm, "end": v(-154, 126.84) * mm, "construction": true});
            skLineSegment(sketch, "E63.bottom", {"start": v(-178.36, 94.5) * mm, "end": v(-129.64, 94.5) * mm});
            skLineSegment(sketch, "E63.top", {"start": v(-178.36, 17.5) * mm, "end": v(-129.64, 17.5) * mm});
            skLineSegment(sketch, "E63.left", {"start": v(-192.5, 80.36) * mm, "end": v(-192.5, 31.64) * mm});
            skLineSegment(sketch, "E63.right", {"start": v(-115.5, 80.36) * mm, "end": v(-115.5, 31.64) * mm});
            skLineSegment(sketch, "E64", {"start": v(-178.36, 17.5) * mm, "end": v(-192.5, 31.64) * mm});
            skLineSegment(sketch, "E65", {"start": v(-178.36, 94.5) * mm, "end": v(-192.5, 80.36) * mm});
            skLineSegment(sketch, "E66", {"start": v(-129.64, 94.5) * mm, "end": v(-115.5, 80.36) * mm});
            skLineSegment(sketch, "E67", {"start": v(-115.5, 31.64) * mm, "end": v(-129.64, 17.5) * mm});
            skPoint(sketch, "E68.orphan", {"position": v(-115.5, 17.5) * mm});
            skPoint(sketch, "E69.orphan", {"position": v(-115.5, 94.5) * mm});
            skPoint(sketch, "E70.orphan", {"position": v(-192.5, 94.5) * mm});
            skPoint(sketch, "E71.orphan", {"position": v(-192.5, 17.5) * mm});
            skLineSegment(sketch, "E72.bottom", {"start": v(-208, 214) * mm, "end": v(-288, 214) * mm, "construction": true});
            skLineSegment(sketch, "E72.top", {"start": v(-208, 294) * mm, "end": v(-288, 294) * mm, "construction": true});
            skLineSegment(sketch, "E72.left", {"start": v(-208, 214) * mm, "end": v(-208, 294) * mm, "construction": true});
            skLineSegment(sketch, "E72.right", {"start": v(-288, 214) * mm, "end": v(-288, 294) * mm, "construction": true});
            skPoint(sketch, "E72.middle", {"position": v(-248, 254) * mm});
            skPoint(sketch, "E73", {"position": v(-283.75, 289.75) * mm});
            skPoint(sketch, "E74", {"position": v(-212.25, 289.75) * mm});
            skPoint(sketch, "E75", {"position": v(-212.25, 218.25) * mm});
            skPoint(sketch, "E76", {"position": v(-283.75, 218.25) * mm});
            skLineSegment(sketch, "E77.bottom", {"start": v(-272.36, 292.5) * mm, "end": v(-223.64, 292.5) * mm});
            skLineSegment(sketch, "E77.top", {"start": v(-272.36, 215.5) * mm, "end": v(-223.64, 215.5) * mm});
            skLineSegment(sketch, "E77.left", {"start": v(-286.5, 278.36) * mm, "end": v(-286.5, 229.64) * mm});
            skLineSegment(sketch, "E77.right", {"start": v(-209.5, 278.36) * mm, "end": v(-209.5, 229.64) * mm});
            skLineSegment(sketch, "E78", {"start": v(-272.36, 215.5) * mm, "end": v(-286.5, 229.64) * mm});
            skLineSegment(sketch, "E79", {"start": v(-272.36, 292.5) * mm, "end": v(-286.5, 278.36) * mm});
            skLineSegment(sketch, "E80", {"start": v(-223.64, 292.5) * mm, "end": v(-209.5, 278.36) * mm});
            skLineSegment(sketch, "E81", {"start": v(-209.5, 229.64) * mm, "end": v(-223.64, 215.5) * mm});
            skPoint(sketch, "E82.orphan", {"position": v(-209.5, 215.5) * mm});
            skPoint(sketch, "E83.orphan", {"position": v(-209.5, 292.5) * mm});
            skPoint(sketch, "E84.orphan", {"position": v(-286.5, 292.5) * mm});
            skPoint(sketch, "E85.orphan", {"position": v(-286.5, 215.5) * mm});
            skSolve(sketch);
        }
        {
            var Q0;
            Q0 = qSketchRegion(id + "F23", true);
            extrude(context, id + "F24", {"entities" : qUnion([Q0]), "operationType" : NewBodyOperationType.REMOVE, "endBound" : BoundingType.THROUGH_ALL, "oppositeDirection" : true, "depth" : 25 * mm});
        }
        {
            var Q0;
            Q0=sQuery(id+"F23.wireOp",VERTEX,"E58");
            var Q1;
            Q1=sQuery(id+"F23.wireOp",VERTEX,"E61");
            var Q2;
            Q2=sQuery(id+"F23.wireOp",VERTEX,"E60");
            var Q3;
            Q3=sQuery(id+"F23.wireOp",VERTEX,"E59");
            var Q4;
            Q4=sQuery(id+"F23.wireOp",VERTEX,"E75");
            var Q5;
            Q5=sQuery(id+"F23.wireOp",VERTEX,"E76");
            var Q6;
            Q6=sQuery(id+"F23.wireOp",VERTEX,"E73");
            var Q7;
            Q7=sQuery(id+"F23.wireOp",VERTEX,"E74");
            var Q8;
            Q8=makeQuery(id+"F3.opExtrude","SWEPT_BODY",BODY,{"disambiguationData":[OSD([sQuery(id+"F0.wireOp",EDGE,"E0.top"),sQuery(id+"F0.wireOp",EDGE,"E1.left"),sQuery(id+"F2.wireOp",EDGE,"E6.bottom"),sQuery(id+"F2.wireOp",EDGE,"E6.top"),sQuery(id+"F2.wireOp",EDGE,"E6.left"),sQuery(id+"F2.wireOp",EDGE,"E6.right")])]});
            hole(context, id + "F25", {"style" : HoleStyle.SIMPLE, "endStyle" : HoleEndStyle.THROUGH, "standardTappedOrClearance" : lookupTablePath({ "standard" : "ISO", "fit" : "Normal", "size" : "M4", "type" : "Clearance" }), "standardBlindInLast" : lookupTablePath({ "fit" : "Standard", "standard" : "ISO", "size" : "M4", "type" : "Clearance" }), "holeDiameter" : 4.4 * mm, "tappedDepth" : 6 * mm, "tapClearance" : 3, "locations" : qUnion([Q0, Q1, Q2, Q3, Q4, Q5, Q6, Q7]), "scope" : qUnion([Q8])});
        }
        {
            var Q0;
            Q0=makeQuery(id+"F1.opExtrude","SWEPT_FACE",FACE,{"disambiguationData":[OSD([sQuery(id+"F0.wireOp",EDGE,"E0.bottom")])]});
            cPlane(context, id + "F26", {"entities" : qUnion([Q0]), "cplaneType" : CPlaneType.OFFSET, "offset" : 15 * mm, "oppositeDirection" : true, "width" : 150 * mm, "height" : 150 * mm});
        }
        {
            var Q0;
            Q0=qCreatedBy(id+"F26.planeOp",FACE);
            var sketch = newSketch(context, id + "F27", { "sketchPlane" : qUnion([Q0])});
            skLineSegment(sketch, "E86.bottom", {"start": v(140, 0) * mm, "end": v(293, 0) * mm});
            skLineSegment(sketch, "E86.top", {"start": v(140, 111) * mm, "end": v(293, 111) * mm});
            skLineSegment(sketch, "E86.left", {"start": v(140, 0) * mm, "end": v(140, 111) * mm});
            skLineSegment(sketch, "E86.right", {"start": v(293, 0) * mm, "end": v(293, 111) * mm});
            skLineSegment(sketch, "E87.bottom", {"start": v(161.16, 96) * mm, "end": v(268.84, 96) * mm});
            skLineSegment(sketch, "E87.top", {"start": v(155, 21) * mm, "end": v(202.69, 21) * mm});
            skLineSegment(sketch, "E87.left", {"start": v(155, 87.43) * mm, "end": v(155, 21) * mm});
            skLineSegment(sketch, "E87.right", {"start": v(275, 87.43) * mm, "end": v(275, 21) * mm});
            skLineSegment(sketch, "E88", {"start": v(155, 96) * mm, "end": v(208.84, 21) * mm, "construction": true});
            skLineSegment(sketch, "E89", {"start": v(268.84, 96) * mm, "end": v(215, 21) * mm});
            skLineSegment(sketch, "E90", {"start": v(215, 21) * mm, "end": v(161.16, 96) * mm});
            skLineSegment(sketch, "E91.trimOffspring", {"start": v(227.31, 21) * mm, "end": v(275, 21) * mm});
            skLineSegment(sketch, "E92", {"start": v(227.31, 21) * mm, "end": v(275, 87.43) * mm});
            skLineSegment(sketch, "E93", {"start": v(275, 96) * mm, "end": v(221.16, 21) * mm, "construction": true});
            skLineSegment(sketch, "E94", {"start": v(155, 87.43) * mm, "end": v(202.69, 21) * mm});
            skSolve(sketch);
        }
        {
            var Q0;
            Q0=makeQuery(id+"F27.imprint","IMPRINT",FACE,{"disambiguationData":[TD([[makeQuery(id+"F27.imprint","IMPRINT",EDGE,{"derivedFrom":sQuery(id+"F27.wireOp",EDGE,"E86.bottom")}),1.0]])]});
            extrude(context, id + "F28", {"entities" : qUnion([Q0]), "oppositeDirection" : true, "depth" : 3 * mm});
        }
        {
            var Q0;
            Q0=makeQuery(id+"F28.opExtrude","CAP_FACE",FACE,{"disambiguationData":[OSD([sQuery(id+"F27.wireOp",EDGE,"E86.bottom"),sQuery(id+"F27.wireOp",EDGE,"E86.top"),sQuery(id+"F27.wireOp",EDGE,"E86.left"),sQuery(id+"F27.wireOp",EDGE,"E86.right"),sQuery(id+"F27.wireOp",EDGE,"E87.bottom"),sQuery(id+"F27.wireOp",EDGE,"E87.top"),sQuery(id+"F27.wireOp",EDGE,"E87.left"),sQuery(id+"F27.wireOp",EDGE,"E87.right")])],"isStart":true});
            var sketch = newSketch(context, id + "F29", { "sketchPlane" : qUnion([Q0])});
            skLineSegment(sketch, "E95.bottom", {"start": v(140, 0) * mm, "end": v(170, 0) * mm});
            skLineSegment(sketch, "E95.top", {"start": v(140, 6) * mm, "end": v(170, 6) * mm});
            skLineSegment(sketch, "E95.left", {"start": v(140, 0) * mm, "end": v(140, 6) * mm});
            skLineSegment(sketch, "E95.right", {"start": v(170, 0) * mm, "end": v(170, 6) * mm});
            skLineSegment(sketch, "E96.1.0.0", {"start": v(202, 0) * mm, "end": v(202, 6) * mm});
            skLineSegment(sketch, "E96.1.0.1", {"start": v(202, 0) * mm, "end": v(232, 0) * mm});
            skLineSegment(sketch, "E96.1.0.2", {"start": v(202, 6) * mm, "end": v(232, 6) * mm});
            skLineSegment(sketch, "E96.1.0.3", {"start": v(232, 0) * mm, "end": v(232, 6) * mm});
            skLineSegment(sketch, "E96.2.0.0", {"start": v(264, 0) * mm, "end": v(264, 6) * mm});
            skLineSegment(sketch, "E96.2.0.1", {"start": v(264, 0) * mm, "end": v(294, 0) * mm});
            skLineSegment(sketch, "E96.2.0.2", {"start": v(264, 6) * mm, "end": v(294, 6) * mm});
            skLineSegment(sketch, "E96.2.0.3", {"start": v(294, 0) * mm, "end": v(294, 6) * mm});
            skLineSegment(sketch, "E96.direction1", {"start": v(140, 0) * mm, "end": v(202, 0) * mm, "construction": true});
            skLineSegment(sketch, "E97.bottom", {"start": v(140, 111) * mm, "end": v(170, 111) * mm});
            skLineSegment(sketch, "E97.top", {"start": v(140, 108) * mm, "end": v(170, 108) * mm});
            skLineSegment(sketch, "E97.left", {"start": v(140, 111) * mm, "end": v(140, 108) * mm});
            skLineSegment(sketch, "E97.right", {"start": v(170, 111) * mm, "end": v(170, 108) * mm});
            skLineSegment(sketch, "E98.1.0.0", {"start": v(230, 111) * mm, "end": v(230, 108) * mm});
            skLineSegment(sketch, "E98.1.0.1", {"start": v(200, 108) * mm, "end": v(230, 108) * mm});
            skLineSegment(sketch, "E98.1.0.2", {"start": v(200, 111) * mm, "end": v(230, 111) * mm});
            skLineSegment(sketch, "E98.1.0.3", {"start": v(200, 111) * mm, "end": v(200, 108) * mm});
            skLineSegment(sketch, "E98.2.0.0", {"start": v(290, 111) * mm, "end": v(290, 108) * mm});
            skLineSegment(sketch, "E98.2.0.1", {"start": v(260, 108) * mm, "end": v(290, 108) * mm});
            skLineSegment(sketch, "E98.2.0.2", {"start": v(260, 111) * mm, "end": v(290, 111) * mm});
            skLineSegment(sketch, "E98.2.0.3", {"start": v(260, 111) * mm, "end": v(260, 108) * mm});
            skLineSegment(sketch, "E98.direction1", {"start": v(170, 108) * mm, "end": v(230, 108) * mm, "construction": true});
            skLineSegment(sketch, "E99.bottom", {"start": v(290, 111) * mm, "end": v(293, 111) * mm});
            skLineSegment(sketch, "E99.top", {"start": v(290, 81) * mm, "end": v(293, 81) * mm});
            skLineSegment(sketch, "E99.left", {"start": v(290, 111) * mm, "end": v(290, 81) * mm});
            skLineSegment(sketch, "E99.right", {"start": v(293, 111) * mm, "end": v(293, 81) * mm});
            skLineSegment(sketch, "E100.0.1.0", {"start": v(290, 51) * mm, "end": v(293, 51) * mm});
            skLineSegment(sketch, "E100.0.1.1", {"start": v(290, 51) * mm, "end": v(290, 21) * mm});
            skLineSegment(sketch, "E100.0.1.2", {"start": v(293, 51) * mm, "end": v(293, 21) * mm});
            skLineSegment(sketch, "E100.0.1.3", {"start": v(290, 21) * mm, "end": v(293, 21) * mm});
            skLineSegment(sketch, "E100.direction1", {"start": v(290, 111) * mm, "end": v(315, 111) * mm, "construction": true});
            skLineSegment(sketch, "E100.direction2", {"start": v(290, 111) * mm, "end": v(290, 51) * mm, "construction": true});
            skSolve(sketch);
        }
        {
            var Q0;
            Q0 = qSketchRegion(id + "F29", true);
            extrude(context, id + "F30", {"entities" : qUnion([Q0]), "operationType" : NewBodyOperationType.REMOVE, "endBound" : BoundingType.THROUGH_ALL, "oppositeDirection" : true, "depth" : 25 * mm});
        }
        {
            var Q0;
            Q0=makeQuery(id+"F28.opExtrude","SWEPT_EDGE",EDGE,{"disambiguationData":[OSD([sQuery(id+"F27.wireOp",EDGE,"E87.bottom"),sQuery(id+"F27.wireOp",EDGE,"E90")])]});
            var Q1;
            Q1=makeQuery(id+"F28.opExtrude","SWEPT_EDGE",EDGE,{"disambiguationData":[OSD([sQuery(id+"F27.wireOp",EDGE,"E87.left"),sQuery(id+"F27.wireOp",EDGE,"E94")])]});
            var Q2;
            Q2=makeQuery(id+"F28.opExtrude","SWEPT_EDGE",EDGE,{"disambiguationData":[OSD([sQuery(id+"F27.wireOp",EDGE,"E89"),sQuery(id+"F27.wireOp",EDGE,"E90")])]});
            var Q3;
            Q3=makeQuery(id+"F28.opExtrude","SWEPT_EDGE",EDGE,{"disambiguationData":[OSD([sQuery(id+"F27.wireOp",EDGE,"E87.top"),sQuery(id+"F27.wireOp",EDGE,"E94")])]});
            var Q4;
            Q4=makeQuery(id+"F28.opExtrude","SWEPT_EDGE",EDGE,{"disambiguationData":[OSD([sQuery(id+"F27.wireOp",EDGE,"E87.top"),sQuery(id+"F27.wireOp",EDGE,"E87.left")])]});
            var Q5;
            Q5=makeQuery(id+"F28.opExtrude","SWEPT_EDGE",EDGE,{"disambiguationData":[OSD([sQuery(id+"F27.wireOp",EDGE,"E91.trimOffspring"),sQuery(id+"F27.wireOp",EDGE,"E92")])]});
            var Q6;
            Q6=makeQuery(id+"F28.opExtrude","SWEPT_EDGE",EDGE,{"disambiguationData":[OSD([sQuery(id+"F27.wireOp",EDGE,"E87.right"),sQuery(id+"F27.wireOp",EDGE,"E91.trimOffspring")])]});
            var Q7;
            Q7=makeQuery(id+"F28.opExtrude","SWEPT_EDGE",EDGE,{"disambiguationData":[OSD([sQuery(id+"F27.wireOp",EDGE,"E87.right"),sQuery(id+"F27.wireOp",EDGE,"E92")])]});
            var Q8;
            Q8=makeQuery(id+"F28.opExtrude","SWEPT_EDGE",EDGE,{"disambiguationData":[OSD([sQuery(id+"F27.wireOp",EDGE,"E87.bottom"),sQuery(id+"F27.wireOp",EDGE,"E89")])]});
            fillet(context, id + "F31", {"entities" : qUnion([Q0, Q1, Q2, Q3, Q4, Q5, Q6, Q7, Q8]), "radius" : 3 * mm, "tangentPropagation" : true, "allowEdgeOverflow" : false});
        }
        {
            var Q0;
            Q0=makeQuery(id+"F28.opExtrude","SWEPT_BODY",BODY,{"disambiguationData":[OSD([sQuery(id+"F27.wireOp",EDGE,"E86.bottom"),sQuery(id+"F27.wireOp",EDGE,"E86.top"),sQuery(id+"F27.wireOp",EDGE,"E86.left"),sQuery(id+"F27.wireOp",EDGE,"E86.right"),sQuery(id+"F27.wireOp",EDGE,"E87.bottom"),sQuery(id+"F27.wireOp",EDGE,"E87.top"),sQuery(id+"F27.wireOp",EDGE,"E87.left"),sQuery(id+"F27.wireOp",EDGE,"E87.right"),sQuery(id+"F27.wireOp",EDGE,"E89"),sQuery(id+"F27.wireOp",EDGE,"E90"),sQuery(id+"F27.wireOp",EDGE,"E91.trimOffspring"),sQuery(id+"F27.wireOp",EDGE,"E92"),sQuery(id+"F27.wireOp",EDGE,"E94")])]});
            transform(context, id + "F32", {"entities" : qUnion([Q0]), "transformType" : TransformType.TRANSLATION_3D, "dx" : 0 * mm, "dy" : (25.4 + 3) * mm, "dz" : 0 * mm, "makeCopy" : true});
        }
        {
            var Q0;
            Q0=makeQuery(id+"F32.opPattern","COPY",BODY,{"derivedFrom":makeQuery(id+"F28.opExtrude","SWEPT_BODY",BODY,{"disambiguationData":[OSD([sQuery(id+"F27.wireOp",EDGE,"E86.bottom"),sQuery(id+"F27.wireOp",EDGE,"E86.top"),sQuery(id+"F27.wireOp",EDGE,"E86.left"),sQuery(id+"F27.wireOp",EDGE,"E86.right"),sQuery(id+"F27.wireOp",EDGE,"E87.bottom"),sQuery(id+"F27.wireOp",EDGE,"E87.top"),sQuery(id+"F27.wireOp",EDGE,"E87.left"),sQuery(id+"F27.wireOp",EDGE,"E87.right"),sQuery(id+"F27.wireOp",EDGE,"E89"),sQuery(id+"F27.wireOp",EDGE,"E90"),sQuery(id+"F27.wireOp",EDGE,"E91.trimOffspring"),sQuery(id+"F27.wireOp",EDGE,"E92"),sQuery(id+"F27.wireOp",EDGE,"E94")])]}),"instanceName":"1"});
            transform(context, id + "F33", {"entities" : qUnion([Q0]), "transformType" : TransformType.TRANSLATION_3D, "dx" : 0 * mm, "dy" : (25.4 + 3) * mm, "dz" : 0 * mm, "makeCopy" : true});
        }
        {
            var Q0;
            Q0=makeQuery(id+"F28.opExtrude","SWEPT_BODY",BODY,{"disambiguationData":[OSD([sQuery(id+"F27.wireOp",EDGE,"E86.bottom"),sQuery(id+"F27.wireOp",EDGE,"E86.top"),sQuery(id+"F27.wireOp",EDGE,"E86.left"),sQuery(id+"F27.wireOp",EDGE,"E86.right"),sQuery(id+"F27.wireOp",EDGE,"E87.bottom"),sQuery(id+"F27.wireOp",EDGE,"E87.top"),sQuery(id+"F27.wireOp",EDGE,"E87.left"),sQuery(id+"F27.wireOp",EDGE,"E87.right")])]});
            var Q1;
            Q1=makeQuery(id+"F32.opPattern","COPY",BODY,{"derivedFrom":makeQuery(id+"F28.opExtrude","SWEPT_BODY",BODY,{"disambiguationData":[OSD([sQuery(id+"F27.wireOp",EDGE,"E86.bottom"),sQuery(id+"F27.wireOp",EDGE,"E86.top"),sQuery(id+"F27.wireOp",EDGE,"E86.left"),sQuery(id+"F27.wireOp",EDGE,"E86.right"),sQuery(id+"F27.wireOp",EDGE,"E87.bottom"),sQuery(id+"F27.wireOp",EDGE,"E87.top"),sQuery(id+"F27.wireOp",EDGE,"E87.left"),sQuery(id+"F27.wireOp",EDGE,"E87.right"),sQuery(id+"F27.wireOp",EDGE,"E89"),sQuery(id+"F27.wireOp",EDGE,"E90"),sQuery(id+"F27.wireOp",EDGE,"E91.trimOffspring"),sQuery(id+"F27.wireOp",EDGE,"E92"),sQuery(id+"F27.wireOp",EDGE,"E94")])]}),"instanceName":"1"});
            var Q2;
            Q2=makeQuery(id+"F33.opPattern","COPY",BODY,{"derivedFrom":makeQuery(id+"F32.opPattern","COPY",BODY,{"derivedFrom":makeQuery(id+"F28.opExtrude","SWEPT_BODY",BODY,{"disambiguationData":[OSD([sQuery(id+"F27.wireOp",EDGE,"E86.bottom"),sQuery(id+"F27.wireOp",EDGE,"E86.top"),sQuery(id+"F27.wireOp",EDGE,"E86.left"),sQuery(id+"F27.wireOp",EDGE,"E86.right"),sQuery(id+"F27.wireOp",EDGE,"E87.bottom"),sQuery(id+"F27.wireOp",EDGE,"E87.top"),sQuery(id+"F27.wireOp",EDGE,"E87.left"),sQuery(id+"F27.wireOp",EDGE,"E87.right"),sQuery(id+"F27.wireOp",EDGE,"E89"),sQuery(id+"F27.wireOp",EDGE,"E90"),sQuery(id+"F27.wireOp",EDGE,"E91.trimOffspring"),sQuery(id+"F27.wireOp",EDGE,"E92"),sQuery(id+"F27.wireOp",EDGE,"E94")])]}),"instanceName":"1"}),"instanceName":"1"});
            var Q3;
            Q3=makeQuery(id+"F1.opExtrude","SWEPT_BODY",BODY,{"disambiguationData":[OSD([sQuery(id+"F0.wireOp",EDGE,"E0.bottom"),sQuery(id+"F0.wireOp",EDGE,"E0.top"),sQuery(id+"F0.wireOp",EDGE,"E0.left"),sQuery(id+"F0.wireOp",EDGE,"E0.right"),sQuery(id+"F0.wireOp",EDGE,"E1.top"),sQuery(id+"F0.wireOp",EDGE,"E1.left"),sQuery(id+"F0.wireOp",EDGE,"E1.right"),sQuery(id+"F0.wireOp",EDGE,"E2.1.0.0"),sQuery(id+"F0.wireOp",EDGE,"E2.1.0.1"),sQuery(id+"F0.wireOp",EDGE,"E2.1.0.2"),sQuery(id+"F0.wireOp",EDGE,"E2.2.0.0"),sQuery(id+"F0.wireOp",EDGE,"E2.2.0.1"),sQuery(id+"F0.wireOp",EDGE,"E2.2.0.2"),sQuery(id+"F0.wireOp",EDGE,"E2.3.0.0"),sQuery(id+"F0.wireOp",EDGE,"E2.3.0.1"),sQuery(id+"F0.wireOp",EDGE,"E3.trimOffspring"),sQuery(id+"F0.wireOp",EDGE,"E4.trimOffspring"),sQuery(id+"F0.wireOp",EDGE,"E5.trimOffspring")])]});
            booleanBodies(context, id + "F34", {"operationType" : BooleanOperationType.SUBTRACTION, "tools" : qUnion([Q0, Q1, Q2]), "targets" : qUnion([Q3]), "keepTools" : true});
        }
        {
            var Q0;
            Q0=makeQuery(id+"F30.boolean.opBoolean","COPY",FACE,{"derivedFrom":makeQuery(id+"F30.opExtrude","SWEPT_FACE",FACE,{"disambiguationData":[OSD([sQuery(id+"F29.wireOp",EDGE,"E97.top")])]})});
            var sketch = newSketch(context, id + "F35", { "sketchPlane" : qUnion([Q0])});
            skLineSegment(sketch, "E101.bottom", {"start": v(140, 15) * mm, "end": v(290, 15) * mm});
            skLineSegment(sketch, "E101.top", {"start": v(140, 74.8) * mm, "end": v(290, 74.8) * mm});
            skLineSegment(sketch, "E101.left", {"start": v(140, 15) * mm, "end": v(140, 74.8) * mm});
            skLineSegment(sketch, "E101.right", {"start": v(290, 15) * mm, "end": v(290, 74.8) * mm});
            skPoint(sketch, "E102", {"position": v(168.5, 24.35) * mm});
            skPoint(sketch, "E103", {"position": v(270.1, 24.35) * mm});
            skPoint(sketch, "E104", {"position": v(210.1, 24.35) * mm});
            skPoint(sketch, "E105", {"position": v(168.5, 52.75) * mm});
            skPoint(sketch, "E106", {"position": v(210.1, 52.75) * mm});
            skPoint(sketch, "E107", {"position": v(270.1, 52.75) * mm});
            skSolve(sketch);
        }
        {
            var Q0;
            Q0 = qSketchRegion(id + "F35", true);
            extrude(context, id + "F36", {"entities" : qUnion([Q0]), "depth" : 3 * mm});
        }
        {
            var Q0;
            Q0=makeQuery(id+"F28.opExtrude","SWEPT_BODY",BODY,{"disambiguationData":[OSD([sQuery(id+"F27.wireOp",EDGE,"E86.bottom"),sQuery(id+"F27.wireOp",EDGE,"E86.top"),sQuery(id+"F27.wireOp",EDGE,"E86.left"),sQuery(id+"F27.wireOp",EDGE,"E86.right"),sQuery(id+"F27.wireOp",EDGE,"E87.bottom"),sQuery(id+"F27.wireOp",EDGE,"E87.top"),sQuery(id+"F27.wireOp",EDGE,"E87.left"),sQuery(id+"F27.wireOp",EDGE,"E87.right"),sQuery(id+"F27.wireOp",EDGE,"E89"),sQuery(id+"F27.wireOp",EDGE,"E90"),sQuery(id+"F27.wireOp",EDGE,"E91.trimOffspring"),sQuery(id+"F27.wireOp",EDGE,"E92"),sQuery(id+"F27.wireOp",EDGE,"E94")])]});
            var Q1;
            Q1=makeQuery(id+"F32.opPattern","COPY",BODY,{"derivedFrom":makeQuery(id+"F28.opExtrude","SWEPT_BODY",BODY,{"disambiguationData":[OSD([sQuery(id+"F27.wireOp",EDGE,"E86.bottom"),sQuery(id+"F27.wireOp",EDGE,"E86.top"),sQuery(id+"F27.wireOp",EDGE,"E86.left"),sQuery(id+"F27.wireOp",EDGE,"E86.right"),sQuery(id+"F27.wireOp",EDGE,"E87.bottom"),sQuery(id+"F27.wireOp",EDGE,"E87.top"),sQuery(id+"F27.wireOp",EDGE,"E87.left"),sQuery(id+"F27.wireOp",EDGE,"E87.right"),sQuery(id+"F27.wireOp",EDGE,"E89"),sQuery(id+"F27.wireOp",EDGE,"E90"),sQuery(id+"F27.wireOp",EDGE,"E91.trimOffspring"),sQuery(id+"F27.wireOp",EDGE,"E92"),sQuery(id+"F27.wireOp",EDGE,"E94")])]}),"instanceName":"1"});
            var Q2;
            Q2=makeQuery(id+"F33.opPattern","COPY",BODY,{"derivedFrom":makeQuery(id+"F32.opPattern","COPY",BODY,{"derivedFrom":makeQuery(id+"F28.opExtrude","SWEPT_BODY",BODY,{"disambiguationData":[OSD([sQuery(id+"F27.wireOp",EDGE,"E86.bottom"),sQuery(id+"F27.wireOp",EDGE,"E86.top"),sQuery(id+"F27.wireOp",EDGE,"E86.left"),sQuery(id+"F27.wireOp",EDGE,"E86.right"),sQuery(id+"F27.wireOp",EDGE,"E87.bottom"),sQuery(id+"F27.wireOp",EDGE,"E87.top"),sQuery(id+"F27.wireOp",EDGE,"E87.left"),sQuery(id+"F27.wireOp",EDGE,"E87.right"),sQuery(id+"F27.wireOp",EDGE,"E89"),sQuery(id+"F27.wireOp",EDGE,"E90"),sQuery(id+"F27.wireOp",EDGE,"E91.trimOffspring"),sQuery(id+"F27.wireOp",EDGE,"E92"),sQuery(id+"F27.wireOp",EDGE,"E94")])]}),"instanceName":"1"}),"instanceName":"1"});
            var Q3;
            Q3=makeQuery(id+"F36.opExtrude","SWEPT_BODY",BODY,{"disambiguationData":[OSD([sQuery(id+"F35.wireOp",EDGE,"E101.bottom"),sQuery(id+"F35.wireOp",EDGE,"E101.top"),sQuery(id+"F35.wireOp",EDGE,"E101.left"),sQuery(id+"F35.wireOp",EDGE,"E101.right")])]});
            booleanBodies(context, id + "F37", {"operationType" : BooleanOperationType.SUBTRACTION, "tools" : qUnion([Q0, Q1, Q2]), "targets" : qUnion([Q3]), "keepTools" : true});
        }
        {
            var Q0;
            Q0=sQuery(id+"F35.wireOp",VERTEX,"E105");
            var Q1;
            Q1=sQuery(id+"F35.wireOp",VERTEX,"E102");
            var Q2;
            Q2=sQuery(id+"F35.wireOp",VERTEX,"E104");
            var Q3;
            Q3=sQuery(id+"F35.wireOp",VERTEX,"E106");
            var Q4;
            Q4=sQuery(id+"F35.wireOp",VERTEX,"E107");
            var Q5;
            Q5=sQuery(id+"F35.wireOp",VERTEX,"E103");
            var Q6;
            Q6=makeQuery(id+"F36.opExtrude","SWEPT_BODY",BODY,{"disambiguationData":[OSD([sQuery(id+"F35.wireOp",EDGE,"E101.bottom"),sQuery(id+"F35.wireOp",EDGE,"E101.top"),sQuery(id+"F35.wireOp",EDGE,"E101.left"),sQuery(id+"F35.wireOp",EDGE,"E101.right")])]});
            hole(context, id + "F38", {"style" : HoleStyle.SIMPLE, "endStyle" : HoleEndStyle.THROUGH, "oppositeDirection" : true, "standardTappedOrClearance" : lookupTablePath({ "standard" : "ISO", "fit" : "Normal", "size" : "M3", "type" : "Clearance" }), "standardBlindInLast" : lookupTablePath({ "fit" : "Standard", "standard" : "ISO", "size" : "M3", "type" : "Clearance" }), "holeDiameter" : 3.3 * mm, "tappedDepth" : 6 * mm, "tapClearance" : 3, "locations" : qUnion([Q0, Q1, Q2, Q3, Q4, Q5]), "scope" : qUnion([Q6])});
        }
        {
            var Q0;
            Q0=makeQuery(id+"F30.boolean.opBoolean","COPY",FACE,{"derivedFrom":makeQuery(id+"F30.opExtrude","SWEPT_FACE",FACE,{"disambiguationData":[OSD([sQuery(id+"F29.wireOp",EDGE,"E99.left")])]})});
            var sketch = newSketch(context, id + "F39", { "sketchPlane" : qUnion([Q0])});
            skLineSegment(sketch, "E108.top", {"start": v(15, 6) * mm, "end": v(74.8, 6) * mm});
            skLineSegment(sketch, "E108.left", {"start": v(15, 111) * mm, "end": v(15, 6) * mm});
            skLineSegment(sketch, "E108.right", {"start": v(74.8, 111) * mm, "end": v(74.8, 6) * mm});
            skLineSegment(sketch, "E109", {"start": v(15, 111) * mm, "end": v(74.8, 111) * mm});
            skSolve(sketch);
        }
        {
            var Q0;
            Q0 = qSketchRegion(id + "F39", true);
            extrude(context, id + "F40", {"entities" : qUnion([Q0]), "depth" : 3 * mm});
        }
        {
            var Q0;
            Q0=makeQuery(id+"F28.opExtrude","SWEPT_BODY",BODY,{"disambiguationData":[OSD([sQuery(id+"F27.wireOp",EDGE,"E86.bottom"),sQuery(id+"F27.wireOp",EDGE,"E86.top"),sQuery(id+"F27.wireOp",EDGE,"E86.left"),sQuery(id+"F27.wireOp",EDGE,"E86.right"),sQuery(id+"F27.wireOp",EDGE,"E87.bottom"),sQuery(id+"F27.wireOp",EDGE,"E87.top"),sQuery(id+"F27.wireOp",EDGE,"E87.left"),sQuery(id+"F27.wireOp",EDGE,"E87.right"),sQuery(id+"F27.wireOp",EDGE,"E89"),sQuery(id+"F27.wireOp",EDGE,"E90"),sQuery(id+"F27.wireOp",EDGE,"E91.trimOffspring"),sQuery(id+"F27.wireOp",EDGE,"E92"),sQuery(id+"F27.wireOp",EDGE,"E94")])]});
            var Q1;
            Q1=makeQuery(id+"F32.opPattern","COPY",BODY,{"derivedFrom":makeQuery(id+"F28.opExtrude","SWEPT_BODY",BODY,{"disambiguationData":[OSD([sQuery(id+"F27.wireOp",EDGE,"E86.bottom"),sQuery(id+"F27.wireOp",EDGE,"E86.top"),sQuery(id+"F27.wireOp",EDGE,"E86.left"),sQuery(id+"F27.wireOp",EDGE,"E86.right"),sQuery(id+"F27.wireOp",EDGE,"E87.bottom"),sQuery(id+"F27.wireOp",EDGE,"E87.top"),sQuery(id+"F27.wireOp",EDGE,"E87.left"),sQuery(id+"F27.wireOp",EDGE,"E87.right"),sQuery(id+"F27.wireOp",EDGE,"E89"),sQuery(id+"F27.wireOp",EDGE,"E90"),sQuery(id+"F27.wireOp",EDGE,"E91.trimOffspring"),sQuery(id+"F27.wireOp",EDGE,"E92"),sQuery(id+"F27.wireOp",EDGE,"E94")])]}),"instanceName":"1"});
            var Q2;
            Q2=makeQuery(id+"F33.opPattern","COPY",BODY,{"derivedFrom":makeQuery(id+"F32.opPattern","COPY",BODY,{"derivedFrom":makeQuery(id+"F28.opExtrude","SWEPT_BODY",BODY,{"disambiguationData":[OSD([sQuery(id+"F27.wireOp",EDGE,"E86.bottom"),sQuery(id+"F27.wireOp",EDGE,"E86.top"),sQuery(id+"F27.wireOp",EDGE,"E86.left"),sQuery(id+"F27.wireOp",EDGE,"E86.right"),sQuery(id+"F27.wireOp",EDGE,"E87.bottom"),sQuery(id+"F27.wireOp",EDGE,"E87.top"),sQuery(id+"F27.wireOp",EDGE,"E87.left"),sQuery(id+"F27.wireOp",EDGE,"E87.right"),sQuery(id+"F27.wireOp",EDGE,"E89"),sQuery(id+"F27.wireOp",EDGE,"E90"),sQuery(id+"F27.wireOp",EDGE,"E91.trimOffspring"),sQuery(id+"F27.wireOp",EDGE,"E92"),sQuery(id+"F27.wireOp",EDGE,"E94")])]}),"instanceName":"1"}),"instanceName":"1"});
            var Q3;
            Q3=makeQuery(id+"F40.opExtrude","SWEPT_BODY",BODY,{"disambiguationData":[OSD([sQuery(id+"F39.wireOp",EDGE,"E108.bottom"),sQuery(id+"F39.wireOp",EDGE,"E108.top"),sQuery(id+"F39.wireOp",EDGE,"E108.left"),sQuery(id+"F39.wireOp",EDGE,"E108.right")])]});
            booleanBodies(context, id + "F41", {"operationType" : BooleanOperationType.SUBTRACTION, "tools" : qUnion([Q0, Q1, Q2]), "targets" : qUnion([Q3]), "keepTools" : true});
        }
        {
            var Q0;
            Q0=makeQuery(id+"F33.opPattern","COPY",FACE,{"derivedFrom":makeQuery(id+"F32.opPattern","COPY",FACE,{"derivedFrom":makeQuery(id+"F28.opExtrude","CAP_FACE",FACE,{"disambiguationData":[OSD([sQuery(id+"F27.wireOp",EDGE,"E86.bottom"),sQuery(id+"F27.wireOp",EDGE,"E86.top"),sQuery(id+"F27.wireOp",EDGE,"E86.left"),sQuery(id+"F27.wireOp",EDGE,"E86.right"),sQuery(id+"F27.wireOp",EDGE,"E87.bottom"),sQuery(id+"F27.wireOp",EDGE,"E87.top"),sQuery(id+"F27.wireOp",EDGE,"E87.left"),sQuery(id+"F27.wireOp",EDGE,"E87.right"),sQuery(id+"F27.wireOp",EDGE,"E89"),sQuery(id+"F27.wireOp",EDGE,"E90"),sQuery(id+"F27.wireOp",EDGE,"E91.trimOffspring"),sQuery(id+"F27.wireOp",EDGE,"E92"),sQuery(id+"F27.wireOp",EDGE,"E94")])],"isStart":false}),"instanceName":"1"}),"instanceName":"1"});
            cPlane(context, id + "F42", {"entities" : qUnion([Q0]), "cplaneType" : CPlaneType.OFFSET, "offset" : 10 * mm, "width" : 150 * mm, "height" : 150 * mm});
        }
        {
            var Q0;
            Q0=qCreatedBy(id+"F42.planeOp",FACE);
            var sketch = newSketch(context, id + "F43", { "sketchPlane" : qUnion([Q0])});
            skLineSegment(sketch, "E110.bottom", {"start": v(-243, 0) * mm, "end": v(-140, 0) * mm});
            skLineSegment(sketch, "E110.top", {"start": v(-243, 79) * mm, "end": v(-140, 79) * mm});
            skLineSegment(sketch, "E110.left", {"start": v(-243, 0) * mm, "end": v(-243, 79) * mm});
            skLineSegment(sketch, "E110.right", {"start": v(-140, 0) * mm, "end": v(-140, 79) * mm});
            skLineSegment(sketch, "E111.bottom", {"start": v(-233, 69) * mm, "end": v(-150, 69) * mm, "construction": true});
            skLineSegment(sketch, "E111.top", {"start": v(-233, 16) * mm, "end": v(-150, 16) * mm, "construction": true});
            skLineSegment(sketch, "E111.left", {"start": v(-233, 69) * mm, "end": v(-233, 16) * mm, "construction": true});
            skLineSegment(sketch, "E111.right", {"start": v(-150, 69) * mm, "end": v(-150, 16) * mm, "construction": true});
            skLineSegment(sketch, "E112", {"start": v(-150, 69) * mm, "end": v(-233, 16) * mm, "construction": true});
            skLineSegment(sketch, "E113", {"start": v(-150, 63.07) * mm, "end": v(-223.7, 16) * mm});
            skLineSegment(sketch, "E114", {"start": v(-233, 21.93) * mm, "end": v(-159.3, 69) * mm});
            skLineSegment(sketch, "E115", {"start": v(-233, 69) * mm, "end": v(-159.3, 69) * mm});
            skLineSegment(sketch, "E116", {"start": v(-233, 21.93) * mm, "end": v(-233, 69) * mm});
            skLineSegment(sketch, "E117", {"start": v(-223.7, 16) * mm, "end": v(-150, 16) * mm});
            skLineSegment(sketch, "E118", {"start": v(-150, 63.07) * mm, "end": v(-150, 16) * mm});
            skSolve(sketch);
        }
        {
            var Q0;
            Q0 = qSketchRegion(id + "F43", true);
            extrude(context, id + "F44", {"entities" : qUnion([Q0]), "depth" : 3 * mm});
        }
        {
            var Q0;
            Q0=makeQuery(id+"F44.opExtrude","CAP_FACE",FACE,{"disambiguationData":[OSD([sQuery(id+"F43.wireOp",EDGE,"E110.bottom"),sQuery(id+"F43.wireOp",EDGE,"E110.top"),sQuery(id+"F43.wireOp",EDGE,"E110.left"),sQuery(id+"F43.wireOp",EDGE,"E110.right"),sQuery(id+"F43.wireOp",EDGE,"E113"),sQuery(id+"F43.wireOp",EDGE,"E114"),sQuery(id+"F43.wireOp",EDGE,"E115"),sQuery(id+"F43.wireOp",EDGE,"E116"),sQuery(id+"F43.wireOp",EDGE,"E117"),sQuery(id+"F43.wireOp",EDGE,"E118")])],"isStart":false});
            var sketch = newSketch(context, id + "F45", { "sketchPlane" : qUnion([Q0])});
            skLineSegment(sketch, "E119.bottom", {"start": v(-140, 0) * mm, "end": v(-160, 0) * mm});
            skLineSegment(sketch, "E119.top", {"start": v(-140, 6) * mm, "end": v(-160, 6) * mm});
            skLineSegment(sketch, "E119.left", {"start": v(-140, 0) * mm, "end": v(-140, 6) * mm});
            skLineSegment(sketch, "E119.right", {"start": v(-160, 0) * mm, "end": v(-160, 6) * mm});
            skLineSegment(sketch, "E120.1.0.0", {"start": v(-182, 0) * mm, "end": v(-182, 6) * mm});
            skLineSegment(sketch, "E120.1.0.1", {"start": v(-182, 6) * mm, "end": v(-202, 6) * mm});
            skLineSegment(sketch, "E120.1.0.2", {"start": v(-202, 0) * mm, "end": v(-202, 6) * mm});
            skLineSegment(sketch, "E120.1.0.3", {"start": v(-182, 0) * mm, "end": v(-202, 0) * mm});
            skLineSegment(sketch, "E120.2.0.0", {"start": v(-224, 0) * mm, "end": v(-224, 6) * mm});
            skLineSegment(sketch, "E120.2.0.1", {"start": v(-224, 6) * mm, "end": v(-244, 6) * mm});
            skLineSegment(sketch, "E120.2.0.2", {"start": v(-244, 0) * mm, "end": v(-244, 6) * mm});
            skLineSegment(sketch, "E120.2.0.3", {"start": v(-224, 0) * mm, "end": v(-244, 0) * mm});
            skLineSegment(sketch, "E120.direction1", {"start": v(-140, 0) * mm, "end": v(-182, 0) * mm, "construction": true});
            skLineSegment(sketch, "E121.bottom", {"start": v(-243, 79) * mm, "end": v(-240, 79) * mm});
            skLineSegment(sketch, "E121.top", {"start": v(-243, 64) * mm, "end": v(-240, 64) * mm});
            skLineSegment(sketch, "E121.left", {"start": v(-243, 79) * mm, "end": v(-243, 64) * mm});
            skLineSegment(sketch, "E121.right", {"start": v(-240, 79) * mm, "end": v(-240, 64) * mm});
            skLineSegment(sketch, "E122.0.1.0", {"start": v(-240, 49) * mm, "end": v(-240, 34) * mm});
            skLineSegment(sketch, "E122.0.1.1", {"start": v(-243, 49) * mm, "end": v(-240, 49) * mm});
            skLineSegment(sketch, "E122.0.1.2", {"start": v(-243, 49) * mm, "end": v(-243, 34) * mm});
            skLineSegment(sketch, "E122.0.1.3", {"start": v(-243, 34) * mm, "end": v(-240, 34) * mm});
            skLineSegment(sketch, "E122.0.2.0", {"start": v(-240, 19) * mm, "end": v(-240, 4) * mm});
            skLineSegment(sketch, "E122.0.2.1", {"start": v(-243, 19) * mm, "end": v(-240, 19) * mm});
            skLineSegment(sketch, "E122.0.2.2", {"start": v(-243, 19) * mm, "end": v(-243, 4) * mm});
            skLineSegment(sketch, "E122.0.2.3", {"start": v(-243, 4) * mm, "end": v(-240, 4) * mm});
            skLineSegment(sketch, "E122.direction1", {"start": v(-265, 64) * mm, "end": v(-240, 64) * mm, "construction": true});
            skLineSegment(sketch, "E122.direction2", {"start": v(-240, 64) * mm, "end": v(-240, 34) * mm, "construction": true});
            skLineSegment(sketch, "E123.bottom", {"start": v(-140, 79) * mm, "end": v(-160, 79) * mm});
            skLineSegment(sketch, "E123.top", {"start": v(-140, 76) * mm, "end": v(-160, 76) * mm});
            skLineSegment(sketch, "E123.left", {"start": v(-140, 79) * mm, "end": v(-140, 76) * mm});
            skLineSegment(sketch, "E123.right", {"start": v(-160, 79) * mm, "end": v(-160, 76) * mm});
            skLineSegment(sketch, "E124.1.0.0", {"start": v(-200, 79) * mm, "end": v(-200, 76) * mm});
            skLineSegment(sketch, "E124.1.0.1", {"start": v(-180, 79) * mm, "end": v(-200, 79) * mm});
            skLineSegment(sketch, "E124.1.0.2", {"start": v(-180, 79) * mm, "end": v(-180, 76) * mm});
            skLineSegment(sketch, "E124.1.0.3", {"start": v(-180, 76) * mm, "end": v(-200, 76) * mm});
            skLineSegment(sketch, "E124.2.0.0", {"start": v(-240, 79) * mm, "end": v(-240, 76) * mm});
            skLineSegment(sketch, "E124.2.0.1", {"start": v(-220, 79) * mm, "end": v(-240, 79) * mm});
            skLineSegment(sketch, "E124.2.0.2", {"start": v(-220, 79) * mm, "end": v(-220, 76) * mm});
            skLineSegment(sketch, "E124.2.0.3", {"start": v(-220, 76) * mm, "end": v(-240, 76) * mm});
            skLineSegment(sketch, "E124.direction1", {"start": v(-160, 76) * mm, "end": v(-200, 76) * mm, "construction": true});
            skSolve(sketch);
        }
        {
            var Q0;
            Q0 = qSketchRegion(id + "F45", true);
            extrude(context, id + "F46", {"entities" : qUnion([Q0]), "operationType" : NewBodyOperationType.REMOVE, "endBound" : BoundingType.THROUGH_ALL, "oppositeDirection" : true, "depth" : 25 * mm});
        }
        {
            var Q0;
            Q0=makeQuery(id+"F44.opExtrude","SWEPT_EDGE",EDGE,{"disambiguationData":[OSD([sQuery(id+"F43.wireOp",EDGE,"E115"),sQuery(id+"F43.wireOp",EDGE,"E116")])]});
            var Q1;
            Q1=makeQuery(id+"F44.opExtrude","SWEPT_EDGE",EDGE,{"disambiguationData":[OSD([sQuery(id+"F43.wireOp",EDGE,"E117"),sQuery(id+"F43.wireOp",EDGE,"E118")])]});
            var Q2;
            Q2=makeQuery(id+"F44.opExtrude","SWEPT_EDGE",EDGE,{"disambiguationData":[OSD([sQuery(id+"F43.wireOp",EDGE,"E113"),sQuery(id+"F43.wireOp",EDGE,"E118")])]});
            var Q3;
            Q3=makeQuery(id+"F44.opExtrude","SWEPT_EDGE",EDGE,{"disambiguationData":[OSD([sQuery(id+"F43.wireOp",EDGE,"E114"),sQuery(id+"F43.wireOp",EDGE,"E116")])]});
            var Q4;
            Q4=makeQuery(id+"F44.opExtrude","SWEPT_EDGE",EDGE,{"disambiguationData":[OSD([sQuery(id+"F43.wireOp",EDGE,"E114"),sQuery(id+"F43.wireOp",EDGE,"E115")])]});
            var Q5;
            Q5=makeQuery(id+"F44.opExtrude","SWEPT_EDGE",EDGE,{"disambiguationData":[OSD([sQuery(id+"F43.wireOp",EDGE,"E113"),sQuery(id+"F43.wireOp",EDGE,"E117")])]});
            fillet(context, id + "F47", {"entities" : qUnion([Q0, Q1, Q2, Q3, Q4, Q5]), "radius" : 3 * mm, "tangentPropagation" : true, "allowEdgeOverflow" : false});
        }
        {
            var Q0;
            Q0=makeQuery(id+"F44.opExtrude","SWEPT_BODY",BODY,{"disambiguationData":[OSD([sQuery(id+"F43.wireOp",EDGE,"E110.bottom"),sQuery(id+"F43.wireOp",EDGE,"E110.top"),sQuery(id+"F43.wireOp",EDGE,"E110.left"),sQuery(id+"F43.wireOp",EDGE,"E110.right"),sQuery(id+"F43.wireOp",EDGE,"E113"),sQuery(id+"F43.wireOp",EDGE,"E114"),sQuery(id+"F43.wireOp",EDGE,"E115"),sQuery(id+"F43.wireOp",EDGE,"E116"),sQuery(id+"F43.wireOp",EDGE,"E117"),sQuery(id+"F43.wireOp",EDGE,"E118")])]});
            transform(context, id + "F48", {"entities" : qUnion([Q0]), "transformType" : TransformType.TRANSLATION_3D, "dx" : 0 * mm, "dy" : (7 + 3) * mm, "dz" : 0 * mm, "makeCopy" : true});
        }
        {
            var Q0;
            Q0=makeQuery(id+"F48.opPattern","COPY",BODY,{"derivedFrom":makeQuery(id+"F44.opExtrude","SWEPT_BODY",BODY,{"disambiguationData":[OSD([sQuery(id+"F43.wireOp",EDGE,"E110.bottom"),sQuery(id+"F43.wireOp",EDGE,"E110.top"),sQuery(id+"F43.wireOp",EDGE,"E110.left"),sQuery(id+"F43.wireOp",EDGE,"E110.right"),sQuery(id+"F43.wireOp",EDGE,"E113"),sQuery(id+"F43.wireOp",EDGE,"E114"),sQuery(id+"F43.wireOp",EDGE,"E115"),sQuery(id+"F43.wireOp",EDGE,"E116"),sQuery(id+"F43.wireOp",EDGE,"E117"),sQuery(id+"F43.wireOp",EDGE,"E118")])]}),"instanceName":"1"});
            transform(context, id + "F49", {"entities" : qUnion([Q0]), "transformType" : TransformType.TRANSLATION_3D, "dx" : 0 * mm, "dy" : (7 + 3) * mm, "dz" : 0 * mm, "makeCopy" : true});
        }
        {
            var Q0;
            Q0=makeQuery(id+"F46.boolean.opBoolean","COPY",FACE,{"derivedFrom":makeQuery(id+"F46.opExtrude","SWEPT_FACE",FACE,{"disambiguationData":[OSD([sQuery(id+"F45.wireOp",EDGE,"E124.2.0.3")])]})});
            var sketch = newSketch(context, id + "F50", { "sketchPlane" : qUnion([Q0])});
            skLineSegment(sketch, "E125.bottom", {"start": v(240, 84.8) * mm, "end": v(140, 84.8) * mm});
            skLineSegment(sketch, "E125.top", {"start": v(240, 107.8) * mm, "end": v(140, 107.8) * mm});
            skLineSegment(sketch, "E125.left", {"start": v(240, 84.8) * mm, "end": v(240, 107.8) * mm});
            skLineSegment(sketch, "E125.right", {"start": v(140, 84.8) * mm, "end": v(140, 107.8) * mm});
            skPoint(sketch, "E126", {"position": v(154, 90.8) * mm});
            skPoint(sketch, "E127", {"position": v(154, 100.8) * mm});
            skPoint(sketch, "E128", {"position": v(230.6, 100.8) * mm});
            skPoint(sketch, "E129", {"position": v(230.6, 90.8) * mm});
            skSolve(sketch);
        }
        {
            var Q0;
            Q0 = qSketchRegion(id + "F50", true);
            extrude(context, id + "F51", {"entities" : qUnion([Q0]), "depth" : 3 * mm});
        }
        {
            var Q0;
            Q0=sQuery(id+"F50.wireOp",VERTEX,"E126");
            var Q1;
            Q1=sQuery(id+"F50.wireOp",VERTEX,"E127");
            var Q2;
            Q2=sQuery(id+"F50.wireOp",VERTEX,"E129");
            var Q3;
            Q3=sQuery(id+"F50.wireOp",VERTEX,"E128");
            var Q4;
            Q4=makeQuery(id+"F51.opExtrude","SWEPT_BODY",BODY,{"disambiguationData":[OSD([sQuery(id+"F50.wireOp",EDGE,"E125.bottom"),sQuery(id+"F50.wireOp",EDGE,"E125.top"),sQuery(id+"F50.wireOp",EDGE,"E125.left"),sQuery(id+"F50.wireOp",EDGE,"E125.right")])]});
            hole(context, id + "F52", {"style" : HoleStyle.SIMPLE, "endStyle" : HoleEndStyle.THROUGH, "oppositeDirection" : true, "standardTappedOrClearance" : lookupTablePath({ "standard" : "ISO", "fit" : "Normal", "size" : "M3", "type" : "Clearance" }), "standardBlindInLast" : lookupTablePath({ "fit" : "Standard", "standard" : "ISO", "size" : "M3", "type" : "Clearance" }), "holeDiameter" : 3.3 * mm, "tappedDepth" : 6 * mm, "tapClearance" : 3, "locations" : qUnion([Q0, Q1, Q2, Q3]), "scope" : qUnion([Q4])});
        }
        {
            var Q0;
            Q0=makeQuery(id+"F48.opPattern","COPY",BODY,{"derivedFrom":makeQuery(id+"F44.opExtrude","SWEPT_BODY",BODY,{"disambiguationData":[OSD([sQuery(id+"F43.wireOp",EDGE,"E110.bottom"),sQuery(id+"F43.wireOp",EDGE,"E110.top"),sQuery(id+"F43.wireOp",EDGE,"E110.left"),sQuery(id+"F43.wireOp",EDGE,"E110.right"),sQuery(id+"F43.wireOp",EDGE,"E113"),sQuery(id+"F43.wireOp",EDGE,"E114"),sQuery(id+"F43.wireOp",EDGE,"E115"),sQuery(id+"F43.wireOp",EDGE,"E116"),sQuery(id+"F43.wireOp",EDGE,"E117"),sQuery(id+"F43.wireOp",EDGE,"E118")])]}),"instanceName":"1"});
            var Q1;
            Q1=makeQuery(id+"F44.opExtrude","SWEPT_BODY",BODY,{"disambiguationData":[OSD([sQuery(id+"F43.wireOp",EDGE,"E110.bottom"),sQuery(id+"F43.wireOp",EDGE,"E110.top"),sQuery(id+"F43.wireOp",EDGE,"E110.left"),sQuery(id+"F43.wireOp",EDGE,"E110.right"),sQuery(id+"F43.wireOp",EDGE,"E113"),sQuery(id+"F43.wireOp",EDGE,"E114"),sQuery(id+"F43.wireOp",EDGE,"E115"),sQuery(id+"F43.wireOp",EDGE,"E116"),sQuery(id+"F43.wireOp",EDGE,"E117"),sQuery(id+"F43.wireOp",EDGE,"E118")])]});
            var Q2;
            Q2=makeQuery(id+"F49.opPattern","COPY",BODY,{"derivedFrom":makeQuery(id+"F48.opPattern","COPY",BODY,{"derivedFrom":makeQuery(id+"F44.opExtrude","SWEPT_BODY",BODY,{"disambiguationData":[OSD([sQuery(id+"F43.wireOp",EDGE,"E110.bottom"),sQuery(id+"F43.wireOp",EDGE,"E110.top"),sQuery(id+"F43.wireOp",EDGE,"E110.left"),sQuery(id+"F43.wireOp",EDGE,"E110.right"),sQuery(id+"F43.wireOp",EDGE,"E113"),sQuery(id+"F43.wireOp",EDGE,"E114"),sQuery(id+"F43.wireOp",EDGE,"E115"),sQuery(id+"F43.wireOp",EDGE,"E116"),sQuery(id+"F43.wireOp",EDGE,"E117"),sQuery(id+"F43.wireOp",EDGE,"E118")])]}),"instanceName":"1"}),"instanceName":"1"});
            var Q3;
            Q3=makeQuery(id+"F51.opExtrude","SWEPT_BODY",BODY,{"disambiguationData":[OSD([sQuery(id+"F50.wireOp",EDGE,"E125.bottom"),sQuery(id+"F50.wireOp",EDGE,"E125.top"),sQuery(id+"F50.wireOp",EDGE,"E125.left"),sQuery(id+"F50.wireOp",EDGE,"E125.right")])]});
            booleanBodies(context, id + "F53", {"operationType" : BooleanOperationType.SUBTRACTION, "tools" : qUnion([Q0, Q1, Q2]), "targets" : qUnion([Q3]), "keepTools" : true});
        }
        {
            var Q0;
            Q0=makeQuery(id+"F44.opExtrude","SWEPT_BODY",BODY,{"disambiguationData":[OSD([sQuery(id+"F43.wireOp",EDGE,"E110.bottom"),sQuery(id+"F43.wireOp",EDGE,"E110.top"),sQuery(id+"F43.wireOp",EDGE,"E110.left"),sQuery(id+"F43.wireOp",EDGE,"E110.right"),sQuery(id+"F43.wireOp",EDGE,"E113"),sQuery(id+"F43.wireOp",EDGE,"E114"),sQuery(id+"F43.wireOp",EDGE,"E115"),sQuery(id+"F43.wireOp",EDGE,"E116"),sQuery(id+"F43.wireOp",EDGE,"E117"),sQuery(id+"F43.wireOp",EDGE,"E118")])]});
            var Q1;
            Q1=makeQuery(id+"F48.opPattern","COPY",BODY,{"derivedFrom":makeQuery(id+"F44.opExtrude","SWEPT_BODY",BODY,{"disambiguationData":[OSD([sQuery(id+"F43.wireOp",EDGE,"E110.bottom"),sQuery(id+"F43.wireOp",EDGE,"E110.top"),sQuery(id+"F43.wireOp",EDGE,"E110.left"),sQuery(id+"F43.wireOp",EDGE,"E110.right"),sQuery(id+"F43.wireOp",EDGE,"E113"),sQuery(id+"F43.wireOp",EDGE,"E114"),sQuery(id+"F43.wireOp",EDGE,"E115"),sQuery(id+"F43.wireOp",EDGE,"E116"),sQuery(id+"F43.wireOp",EDGE,"E117"),sQuery(id+"F43.wireOp",EDGE,"E118")])]}),"instanceName":"1"});
            var Q2;
            Q2=makeQuery(id+"F49.opPattern","COPY",BODY,{"derivedFrom":makeQuery(id+"F48.opPattern","COPY",BODY,{"derivedFrom":makeQuery(id+"F44.opExtrude","SWEPT_BODY",BODY,{"disambiguationData":[OSD([sQuery(id+"F43.wireOp",EDGE,"E110.bottom"),sQuery(id+"F43.wireOp",EDGE,"E110.top"),sQuery(id+"F43.wireOp",EDGE,"E110.left"),sQuery(id+"F43.wireOp",EDGE,"E110.right"),sQuery(id+"F43.wireOp",EDGE,"E113"),sQuery(id+"F43.wireOp",EDGE,"E114"),sQuery(id+"F43.wireOp",EDGE,"E115"),sQuery(id+"F43.wireOp",EDGE,"E116"),sQuery(id+"F43.wireOp",EDGE,"E117"),sQuery(id+"F43.wireOp",EDGE,"E118")])]}),"instanceName":"1"}),"instanceName":"1"});
            var Q3;
            Q3=makeQuery(id+"F1.opExtrude","SWEPT_BODY",BODY,{"disambiguationData":[OSD([sQuery(id+"F0.wireOp",EDGE,"E0.bottom"),sQuery(id+"F0.wireOp",EDGE,"E0.top"),sQuery(id+"F0.wireOp",EDGE,"E0.left"),sQuery(id+"F0.wireOp",EDGE,"E0.right"),sQuery(id+"F0.wireOp",EDGE,"E1.top"),sQuery(id+"F0.wireOp",EDGE,"E1.left"),sQuery(id+"F0.wireOp",EDGE,"E1.right"),sQuery(id+"F0.wireOp",EDGE,"E2.1.0.0"),sQuery(id+"F0.wireOp",EDGE,"E2.1.0.1"),sQuery(id+"F0.wireOp",EDGE,"E2.1.0.2"),sQuery(id+"F0.wireOp",EDGE,"E2.2.0.0"),sQuery(id+"F0.wireOp",EDGE,"E2.2.0.1"),sQuery(id+"F0.wireOp",EDGE,"E2.2.0.2"),sQuery(id+"F0.wireOp",EDGE,"E2.3.0.0"),sQuery(id+"F0.wireOp",EDGE,"E2.3.0.1"),sQuery(id+"F0.wireOp",EDGE,"E3.trimOffspring"),sQuery(id+"F0.wireOp",EDGE,"E4.trimOffspring"),sQuery(id+"F0.wireOp",EDGE,"E5.trimOffspring")])]});
            booleanBodies(context, id + "F54", {"operationType" : BooleanOperationType.SUBTRACTION, "tools" : qUnion([Q0, Q1, Q2]), "targets" : qUnion([Q3]), "keepTools" : true});
        }
        {
            var Q0;
            Q0=makeQuery(id+"F46.boolean.opBoolean","COPY",FACE,{"derivedFrom":makeQuery(id+"F46.opExtrude","SWEPT_FACE",FACE,{"disambiguationData":[OSD([sQuery(id+"F45.wireOp",EDGE,"E122.0.2.0")])]})});
            var sketch = newSketch(context, id + "F55", { "sketchPlane" : qUnion([Q0])});
            skLineSegment(sketch, "E130.bottom", {"start": v(84.8, 79) * mm, "end": v(107.8, 79) * mm});
            skLineSegment(sketch, "E130.top", {"start": v(84.8, 6) * mm, "end": v(107.8, 6) * mm});
            skLineSegment(sketch, "E130.left", {"start": v(84.8, 79) * mm, "end": v(84.8, 6) * mm});
            skLineSegment(sketch, "E130.right", {"start": v(107.8, 79) * mm, "end": v(107.8, 6) * mm});
            skSolve(sketch);
        }
        {
            var Q0;
            Q0 = qSketchRegion(id + "F55", true);
            extrude(context, id + "F56", {"entities" : qUnion([Q0]), "depth" : 3 * mm});
        }
        {
            var Q0;
            Q0=makeQuery(id+"F44.opExtrude","SWEPT_BODY",BODY,{"disambiguationData":[OSD([sQuery(id+"F43.wireOp",EDGE,"E110.bottom"),sQuery(id+"F43.wireOp",EDGE,"E110.top"),sQuery(id+"F43.wireOp",EDGE,"E110.left"),sQuery(id+"F43.wireOp",EDGE,"E110.right"),sQuery(id+"F43.wireOp",EDGE,"E113"),sQuery(id+"F43.wireOp",EDGE,"E114"),sQuery(id+"F43.wireOp",EDGE,"E115"),sQuery(id+"F43.wireOp",EDGE,"E116"),sQuery(id+"F43.wireOp",EDGE,"E117"),sQuery(id+"F43.wireOp",EDGE,"E118")])]});
            var Q1;
            Q1=makeQuery(id+"F48.opPattern","COPY",BODY,{"derivedFrom":makeQuery(id+"F44.opExtrude","SWEPT_BODY",BODY,{"disambiguationData":[OSD([sQuery(id+"F43.wireOp",EDGE,"E110.bottom"),sQuery(id+"F43.wireOp",EDGE,"E110.top"),sQuery(id+"F43.wireOp",EDGE,"E110.left"),sQuery(id+"F43.wireOp",EDGE,"E110.right"),sQuery(id+"F43.wireOp",EDGE,"E113"),sQuery(id+"F43.wireOp",EDGE,"E114"),sQuery(id+"F43.wireOp",EDGE,"E115"),sQuery(id+"F43.wireOp",EDGE,"E116"),sQuery(id+"F43.wireOp",EDGE,"E117"),sQuery(id+"F43.wireOp",EDGE,"E118")])]}),"instanceName":"1"});
            var Q2;
            Q2=makeQuery(id+"F49.opPattern","COPY",BODY,{"derivedFrom":makeQuery(id+"F48.opPattern","COPY",BODY,{"derivedFrom":makeQuery(id+"F44.opExtrude","SWEPT_BODY",BODY,{"disambiguationData":[OSD([sQuery(id+"F43.wireOp",EDGE,"E110.bottom"),sQuery(id+"F43.wireOp",EDGE,"E110.top"),sQuery(id+"F43.wireOp",EDGE,"E110.left"),sQuery(id+"F43.wireOp",EDGE,"E110.right"),sQuery(id+"F43.wireOp",EDGE,"E113"),sQuery(id+"F43.wireOp",EDGE,"E114"),sQuery(id+"F43.wireOp",EDGE,"E115"),sQuery(id+"F43.wireOp",EDGE,"E116"),sQuery(id+"F43.wireOp",EDGE,"E117"),sQuery(id+"F43.wireOp",EDGE,"E118")])]}),"instanceName":"1"}),"instanceName":"1"});
            var Q3;
            Q3=makeQuery(id+"F56.opExtrude","SWEPT_BODY",BODY,{"disambiguationData":[OSD([sQuery(id+"F55.wireOp",EDGE,"E130.bottom"),sQuery(id+"F55.wireOp",EDGE,"E130.top"),sQuery(id+"F55.wireOp",EDGE,"E130.left"),sQuery(id+"F55.wireOp",EDGE,"E130.right")])]});
            booleanBodies(context, id + "F57", {"operationType" : BooleanOperationType.SUBTRACTION, "tools" : qUnion([Q0, Q1, Q2]), "targets" : qUnion([Q3]), "keepTools" : true});
        }
    });
